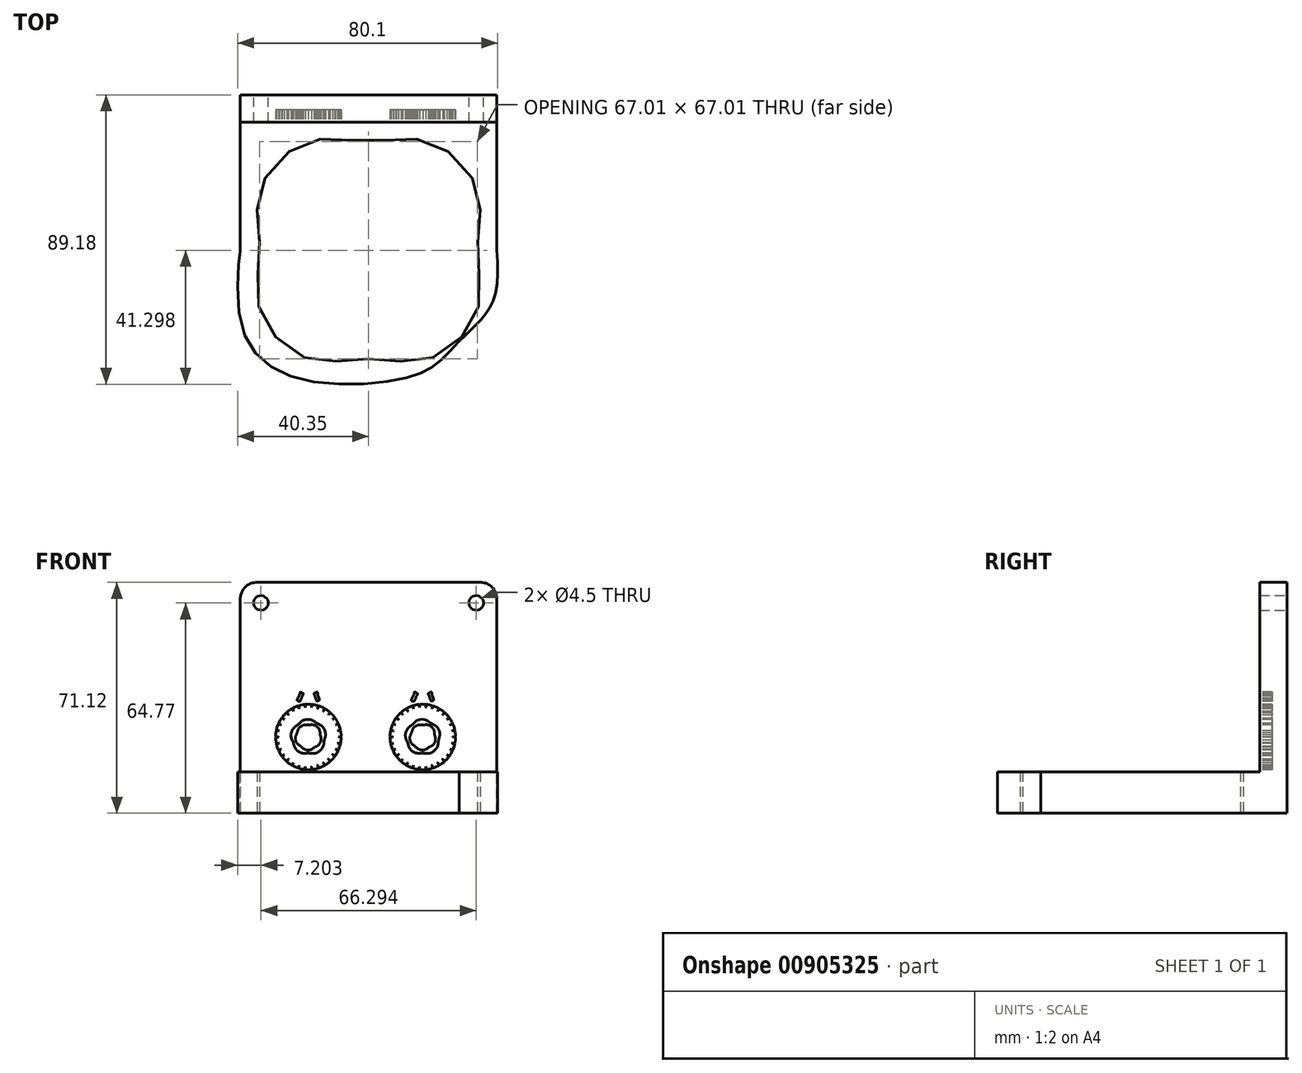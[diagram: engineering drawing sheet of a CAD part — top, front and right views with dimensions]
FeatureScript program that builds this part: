
annotation { "Feature Type Name" : "Feature", "Feature Type Description" : "" }
export const myFeature = defineFeature(function(context is Context, id is Id, definition is map)
    precondition{}
    {
        {
            var Q0;
            Q0=qCreatedBy(makeId("Top.planeOp"),FACE);
            var sketch = newSketch(context, id + "F0", { "sketchPlane" : qUnion([Q0])});
            skFitSpline(sketch, "E0", {"points": [v(-39.5, 39.5) * mm, v(-39.5, 39.5) * mm, v(-39.5, 39.5) * mm, v(-39.5, 38.98) * mm, v(-39.5, 0) * mm, v(-39.5, 0) * mm, v(-39.5, 0) * mm, v(-39.5, -21.82) * mm, v(-21.8, -39.5) * mm, v(10.9, -39.5) * mm, v(20.78, -35.08) * mm, v(27.93, -27.93) * mm]});
            skFitSpline(sketch, "E1", {"points": [v(27.93, -27.93) * mm, v(35.08, -20.78) * mm, v(39.5, -10.91) * mm, v(39.5, 0) * mm, v(39.5, 0) * mm, v(39.5, 0) * mm, v(39.5, 38.98) * mm, v(39.5, 39.5) * mm, v(39.5, 39.5) * mm, v(39.5, 39.5) * mm]});
            skFitSpline(sketch, "E2", {"points": [v(39.5, 39.5) * mm, v(39.5, 39.5) * mm, v(39.5, 39.5) * mm, v(38.99, 39.5) * mm, v(-38.99, 39.5) * mm, v(-39.5, 39.5) * mm, v(-39.5, 39.5) * mm, v(-39.5, 39.5) * mm]});
            skFitSpline(sketch, "E3", {"points": [v(0, -33.5) * mm, v(-18.5, -33.5) * mm, v(-33.5, -18.5) * mm, v(-33.5, 0) * mm, v(-33.5, 18.5) * mm, v(-18.5, 33.5) * mm, v(0, 33.5) * mm, v(18.5, 33.5) * mm, v(33.5, 18.5) * mm, v(33.5, 0) * mm, v(33.5, -18.5) * mm, v(18.5, -33.5) * mm, v(0, -33.5) * mm]});
            skSolve(sketch);
        }
        {
            var Q0;
            Q0=makeQuery(id+"F0.imprint","IMPRINT",FACE,{"disambiguationData":[TD([[makeQuery(id+"F0.imprint","IMPRINT",EDGE,{"derivedFrom":sQuery(id+"F0.wireOp",EDGE,"E0")}),1.0]])]});
            extrude(context, id + "F1", {"entities" : qUnion([Q0]), "depth" : 12.7 * mm, "offsetDistance" : 25.4 * mm});
        }
        {
            var Q0;
            Q0=makeQuery(id+"F1.opExtrude","SWEPT_FACE",FACE,{"disambiguationData":[OSD([sQuery(id+"F0.wireOp",EDGE,"E2")])]});
            var sketch = newSketch(context, id + "F2", { "sketchPlane" : qUnion([Q0])});
            skLineSegment(sketch, "E4.bottom", {"start": v(-39.5, 0) * mm, "end": v(39.5, 0) * mm});
            skLineSegment(sketch, "E4.top", {"start": v(-39.5, 71.12) * mm, "end": v(39.5, 71.12) * mm});
            skLineSegment(sketch, "E4.left", {"start": v(-39.5, 0) * mm, "end": v(-39.5, 71.12) * mm});
            skLineSegment(sketch, "E4.right", {"start": v(39.5, 0) * mm, "end": v(39.5, 71.12) * mm});
            skSolve(sketch);
        }
        {
            var Q0;
            {var subQ0=sQuery(id+"F2.wireOp",EDGE,"E4.top");Q0=makeQuery(id+"F2.imprint","IMPRINT",FACE,{"disambiguationData":[TD([[makeQuery(id+"F2.imprint","IMPRINT",EDGE,{"derivedFrom":subQ0}),-1.0]])]});}
            var Q1;
            {var subQ0=sQuery(id+"F2.wireOp",EDGE,"E4.bottom");Q1=makeQuery(id+"F2.imprint","IMPRINT",FACE,{"disambiguationData":[TD([[makeQuery(id+"F2.imprint","IMPRINT",EDGE,{"derivedFrom":subQ0}),1.0]])]});}
            extrude(context, id + "F3", {"entities" : qUnion([Q0, Q1]), "operationType" : NewBodyOperationType.ADD, "depth" : 8.38 * mm, "offsetDistance" : 25.4 * mm});
        }
        {
            var Q0;
            Q0=makeQuery(id+"F3.opExtrude","CAP_FACE",FACE,{"disambiguationData":[OSD([sQuery(id+"F2.wireOp",EDGE,"E4.bottom"),sQuery(id+"F2.wireOp",EDGE,"E4.top"),sQuery(id+"F2.wireOp",EDGE,"E4.left"),sQuery(id+"F2.wireOp",EDGE,"E4.right")])],"isStart":true});
            var sketch = newSketch(context, id + "F4", { "sketchPlane" : qUnion([Q0])});
            skFitSpline(sketch, "E5", {"points": [v(-16.3, 37.14) * mm, v(-16.53, 37.06) * mm, v(-16.78, 36.97) * mm, v(-16.74, 36.67) * mm]});
            skFitSpline(sketch, "E6", {"points": [v(-16.74, 36.67) * mm, v(-16.73, 36.54) * mm, v(-16.65, 36.4) * mm, v(-16.61, 36.28) * mm]});
            skFitSpline(sketch, "E7", {"points": [v(-16.61, 36.28) * mm, v(-16.45, 35.85) * mm, v(-16.3, 35.4) * mm, v(-16.13, 34.98) * mm]});
            skFitSpline(sketch, "E8", {"points": [v(-16.13, 34.98) * mm, v(-16.07, 34.8) * mm, v(-15.98, 34.64) * mm, v(-15.77, 34.63) * mm]});
            skFitSpline(sketch, "E9", {"points": [v(-15.77, 34.63) * mm, v(-15.54, 34.61) * mm, v(-15.22, 34.78) * mm, v(-15.19, 35.01) * mm]});
            skFitSpline(sketch, "E10", {"points": [v(-15.19, 35.01) * mm, v(-15.17, 35.15) * mm, v(-15.24, 35.3) * mm, v(-15.29, 35.42) * mm]});
            skFitSpline(sketch, "E11", {"points": [v(-15.29, 35.42) * mm, v(-15.37, 35.65) * mm, v(-15.46, 35.88) * mm, v(-15.54, 36.11) * mm]});
            skFitSpline(sketch, "E12", {"points": [v(-15.54, 36.11) * mm, v(-15.65, 36.42) * mm, v(-15.81, 37.32) * mm, v(-16.3, 37.14) * mm]});
            skFitSpline(sketch, "E13", {"points": [v(-20.56, 37.1) * mm, v(-21.01, 37.32) * mm, v(-21.2, 36.62) * mm, v(-21.33, 36.34) * mm]});
            skFitSpline(sketch, "E14", {"points": [v(-21.33, 36.34) * mm, v(-21.5, 35.98) * mm, v(-21.7, 35.63) * mm, v(-21.83, 35.26) * mm]});
            skFitSpline(sketch, "E15", {"points": [v(-21.83, 35.26) * mm, v(-22, 34.76) * mm, v(-21.22, 34.43) * mm, v(-20.96, 34.89) * mm]});
            skFitSpline(sketch, "E16", {"points": [v(-20.96, 34.89) * mm, v(-20.75, 35.26) * mm, v(-20.6, 35.68) * mm, v(-20.41, 36.06) * mm]});
            skFitSpline(sketch, "E17", {"points": [v(-20.41, 36.06) * mm, v(-20.34, 36.21) * mm, v(-20.25, 36.37) * mm, v(-20.2, 36.52) * mm, v(-20.08, 36.85) * mm, v(-20.3, 36.99) * mm, v(-20.56, 37.1) * mm]});
            skFitSpline(sketch, "E18", {"points": [v(-19.4, 35.5) * mm, v(-18.9, 35.5) * mm, v(-18.4, 35.5) * mm, v(-17.91, 35.5) * mm, v(-17.84, 35.5) * mm, v(-17.7, 35.47) * mm, v(-17.63, 35.5) * mm]});
            skFitSpline(sketch, "E19", {"points": [v(-17.63, 35.5) * mm, v(-17.56, 35.53) * mm, v(-17.6, 35.5) * mm, v(-17.56, 35.58) * mm]});
            skFitSpline(sketch, "E20", {"points": [v(-17.56, 35.58) * mm, v(-17.43, 35.76) * mm, v(-17.38, 36.08) * mm, v(-17.3, 36.29) * mm]});
            skFitSpline(sketch, "E21", {"points": [v(-17.3, 36.29) * mm, v(-17.43, 36.29) * mm, v(-17.55, 36.29) * mm, v(-17.68, 36.29) * mm]});
            skFitSpline(sketch, "E22", {"points": [v(-17.68, 36.29) * mm, v(-17.57, 36.66) * mm, v(-17.65, 37.16) * mm, v(-17.65, 37.54) * mm, v(-17.65, 37.95) * mm, v(-17.58, 38.43) * mm, v(-17.67, 38.83) * mm]});
            skFitSpline(sketch, "E23", {"points": [v(-17.67, 38.83) * mm, v(-17.75, 39.18) * mm, v(-18.06, 39.26) * mm, v(-18.38, 39.26) * mm, v(-18.65, 39.26) * mm, v(-18.96, 39.3) * mm, v(-19.16, 39.1) * mm]});
            skFitSpline(sketch, "E24", {"points": [v(-19.16, 39.1) * mm, v(-19.45, 38.8) * mm, v(-19.33, 38.14) * mm, v(-19.33, 37.78) * mm, v(-19.33, 37.47) * mm, v(-19.33, 37.16) * mm, v(-19.33, 36.85) * mm, v(-19.33, 36.68) * mm, v(-19.35, 36.46) * mm, v(-19.3, 36.29) * mm]});
            skFitSpline(sketch, "E25", {"points": [v(-19.3, 36.29) * mm, v(-19.42, 36.29) * mm, v(-19.55, 36.29) * mm, v(-19.67, 36.29) * mm]});
            skFitSpline(sketch, "E26", {"points": [v(-19.67, 36.29) * mm, v(-19.58, 36.03) * mm, v(-19.49, 35.76) * mm, v(-19.4, 35.5) * mm]});
            skFitSpline(sketch, "E27", {"points": [v(18.87, 37.14) * mm, v(18.64, 37.06) * mm, v(18.4, 36.97) * mm, v(18.43, 36.67) * mm]});
            skFitSpline(sketch, "E28", {"points": [v(18.43, 36.67) * mm, v(18.44, 36.54) * mm, v(18.52, 36.4) * mm, v(18.56, 36.28) * mm]});
            skFitSpline(sketch, "E29", {"points": [v(18.56, 36.28) * mm, v(18.72, 35.85) * mm, v(18.87, 35.4) * mm, v(19.04, 34.98) * mm]});
            skFitSpline(sketch, "E30", {"points": [v(19.04, 34.98) * mm, v(19.1, 34.8) * mm, v(19.2, 34.64) * mm, v(19.4, 34.63) * mm]});
            skFitSpline(sketch, "E31", {"points": [v(19.4, 34.63) * mm, v(19.63, 34.61) * mm, v(19.95, 34.78) * mm, v(19.98, 35.01) * mm]});
            skFitSpline(sketch, "E32", {"points": [v(19.98, 35.01) * mm, v(20, 35.15) * mm, v(19.93, 35.3) * mm, v(19.88, 35.42) * mm]});
            skFitSpline(sketch, "E33", {"points": [v(19.88, 35.42) * mm, v(19.8, 35.65) * mm, v(19.72, 35.88) * mm, v(19.63, 36.11) * mm]});
            skFitSpline(sketch, "E34", {"points": [v(19.63, 36.11) * mm, v(19.52, 36.42) * mm, v(19.36, 37.32) * mm, v(18.87, 37.14) * mm]});
            skFitSpline(sketch, "E35", {"points": [v(14.6, 37.1) * mm, v(14.16, 37.32) * mm, v(13.97, 36.62) * mm, v(13.84, 36.34) * mm, v(13.68, 35.98) * mm, v(13.47, 35.63) * mm, v(13.34, 35.26) * mm]});
            skFitSpline(sketch, "E36", {"points": [v(13.34, 35.26) * mm, v(13.16, 34.76) * mm, v(13.95, 34.43) * mm, v(14.21, 34.89) * mm]});
            skFitSpline(sketch, "E37", {"points": [v(14.21, 34.89) * mm, v(14.42, 35.26) * mm, v(14.58, 35.68) * mm, v(14.76, 36.06) * mm, v(14.83, 36.21) * mm, v(14.92, 36.37) * mm, v(14.97, 36.52) * mm, v(15.09, 36.85) * mm, v(14.87, 36.99) * mm, v(14.6, 37.1) * mm]});
            skFitSpline(sketch, "E38", {"points": [v(15.78, 35.5) * mm, v(16.27, 35.5) * mm, v(16.77, 35.5) * mm, v(17.26, 35.5) * mm, v(17.33, 35.5) * mm, v(17.47, 35.47) * mm, v(17.54, 35.5) * mm]});
            skFitSpline(sketch, "E39", {"points": [v(17.54, 35.5) * mm, v(17.61, 35.53) * mm, v(17.56, 35.5) * mm, v(17.62, 35.58) * mm]});
            skFitSpline(sketch, "E40", {"points": [v(17.62, 35.58) * mm, v(17.75, 35.76) * mm, v(17.8, 36.08) * mm, v(17.87, 36.29) * mm]});
            skFitSpline(sketch, "E41", {"points": [v(17.87, 36.29) * mm, v(17.74, 36.29) * mm, v(17.62, 36.29) * mm, v(17.5, 36.29) * mm]});
            skFitSpline(sketch, "E42", {"points": [v(17.5, 36.29) * mm, v(17.6, 36.66) * mm, v(17.52, 37.16) * mm, v(17.52, 37.54) * mm, v(17.52, 37.95) * mm, v(17.6, 38.43) * mm, v(17.5, 38.83) * mm]});
            skFitSpline(sketch, "E43", {"points": [v(17.5, 38.83) * mm, v(17.42, 39.18) * mm, v(17.1, 39.26) * mm, v(16.8, 39.26) * mm, v(16.53, 39.26) * mm, v(16.22, 39.3) * mm, v(16, 39.1) * mm]});
            skFitSpline(sketch, "E44", {"points": [v(16, 39.1) * mm, v(15.73, 38.8) * mm, v(15.85, 38.14) * mm, v(15.85, 37.78) * mm, v(15.85, 37.47) * mm, v(15.85, 37.16) * mm, v(15.85, 36.85) * mm, v(15.85, 36.68) * mm, v(15.82, 36.46) * mm, v(15.87, 36.29) * mm]});
            skFitSpline(sketch, "E45", {"points": [v(15.87, 36.29) * mm, v(15.75, 36.29) * mm, v(15.62, 36.29) * mm, v(15.5, 36.29) * mm]});
            skFitSpline(sketch, "E46", {"points": [v(15.5, 36.29) * mm, v(15.6, 36.03) * mm, v(15.68, 35.76) * mm, v(15.78, 35.5) * mm]});
            skFitSpline(sketch, "E47", {"points": [v(-25.13, 35.02) * mm, v(-24.72, 36.98) * mm, v(-23.7, 39.03) * mm, v(-22.15, 40.32) * mm]});
            skFitSpline(sketch, "E48", {"points": [v(-22.15, 40.32) * mm, v(-20.8, 41.44) * mm, v(-19.07, 41.82) * mm, v(-17.35, 41.52) * mm]});
            skFitSpline(sketch, "E49", {"points": [v(-17.35, 41.52) * mm, v(-15.7, 41.24) * mm, v(-14.3, 40.3) * mm, v(-13.36, 38.94) * mm]});
            skFitSpline(sketch, "E50", {"points": [v(-13.36, 38.94) * mm, v(-12.68, 37.95) * mm, v(-12.2, 36.77) * mm, v(-12.02, 35.57) * mm]});
            skFitSpline(sketch, "E51", {"points": [v(-12.02, 35.57) * mm, v(-12, 35.46) * mm, v(-12.03, 35.14) * mm, v(-11.97, 35.05) * mm]});
            skFitSpline(sketch, "E52", {"points": [v(-11.97, 35.05) * mm, v(-11.91, 34.96) * mm, v(-11.5, 35.02) * mm, v(-11.38, 35.02) * mm, v(-11.04, 35.02) * mm, v(-10.7, 35.02) * mm, v(-10.35, 35.02) * mm, v(-10.3, 35.02) * mm, v(-10.13, 34.99) * mm, v(-10.1, 35.02) * mm]});
            skFitSpline(sketch, "E53", {"points": [v(-10.1, 35.02) * mm, v(-10.05, 35.05) * mm, v(-10.08, 35.27) * mm, v(-10.08, 35.34) * mm, v(-10.08, 35.67) * mm, v(-10.14, 35.66) * mm, v(-9.86, 35.66) * mm, v(-9.58, 35.66) * mm, v(-9.3, 35.66) * mm, v(-9.01, 35.66) * mm, v(-7.96, 35.66) * mm, v(-6.9, 35.66) * mm, v(-5.85, 35.66) * mm, v(-2.95, 35.66) * mm, v(-0.06, 35.66) * mm, v(2.84, 35.66) * mm, v(4.06, 35.66) * mm, v(5.28, 35.66) * mm, v(6.5, 35.66) * mm, v(6.91, 35.66) * mm, v(7.32, 35.66) * mm, v(7.72, 35.66) * mm, v(7.91, 35.66) * mm, v(8.21, 35.72) * mm, v(8.4, 35.66) * mm]});
            skFitSpline(sketch, "E54", {"points": [v(8.4, 35.66) * mm, v(8.42, 35.65) * mm, v(8.46, 35.67) * mm, v(8.48, 35.65) * mm]});
            skFitSpline(sketch, "E55", {"points": [v(8.48, 35.65) * mm, v(8.6, 35.55) * mm, v(8.37, 35.1) * mm, v(8.5, 35.02) * mm]});
            skFitSpline(sketch, "E56", {"points": [v(8.5, 35.02) * mm, v(8.56, 34.98) * mm, v(8.76, 35.02) * mm, v(8.82, 35.02) * mm, v(9, 35.02) * mm, v(9.2, 35.02) * mm, v(9.38, 35.02) * mm, v(9.55, 35.02) * mm, v(9.72, 35.02) * mm, v(9.89, 35.02) * mm, v(9.95, 35.02) * mm, v(10.16, 34.98) * mm, v(10.21, 35.02) * mm]});
            skFitSpline(sketch, "E57", {"points": [v(10.21, 35.02) * mm, v(10.28, 35.07) * mm, v(10.27, 35.35) * mm, v(10.28, 35.45) * mm]});
            skFitSpline(sketch, "E58", {"points": [v(10.28, 35.45) * mm, v(10.34, 35.85) * mm, v(10.43, 36.24) * mm, v(10.54, 36.63) * mm]});
            skFitSpline(sketch, "E59", {"points": [v(10.54, 36.63) * mm, v(10.87, 37.8) * mm, v(11.43, 38.94) * mm, v(12.29, 39.83) * mm]});
            skFitSpline(sketch, "E60", {"points": [v(12.29, 39.83) * mm, v(13.43, 41.03) * mm, v(15.01, 41.59) * mm, v(16.65, 41.62) * mm]});
            skFitSpline(sketch, "E61", {"points": [v(16.65, 41.62) * mm, v(18.33, 41.65) * mm, v(19.99, 41.16) * mm, v(21.2, 39.97) * mm]});
            skFitSpline(sketch, "E62", {"points": [v(21.2, 39.97) * mm, v(22.1, 39.1) * mm, v(22.7, 37.96) * mm, v(23.05, 36.77) * mm]});
            skFitSpline(sketch, "E63", {"points": [v(23.05, 36.77) * mm, v(23.17, 36.36) * mm, v(23.26, 35.95) * mm, v(23.33, 35.53) * mm, v(23.34, 35.45) * mm, v(23.33, 35.07) * mm, v(23.4, 35.02) * mm]});
            skFitSpline(sketch, "E64", {"points": [v(23.4, 35.02) * mm, v(23.47, 34.95) * mm, v(23.94, 35.02) * mm, v(24.04, 35.02) * mm, v(24.34, 35.02) * mm, v(24.73, 34.95) * mm, v(25.02, 35.02) * mm]});
            skFitSpline(sketch, "E65", {"points": [v(25.02, 35.02) * mm, v(25.14, 35.05) * mm, v(25.12, 35.05) * mm, v(25.21, 35.17) * mm]});
            skFitSpline(sketch, "E66", {"points": [v(25.21, 35.17) * mm, v(25.37, 35.38) * mm, v(25.55, 35.58) * mm, v(25.75, 35.76) * mm]});
            skFitSpline(sketch, "E67", {"points": [v(25.75, 35.76) * mm, v(26.44, 36.37) * mm, v(27.31, 36.73) * mm, v(28.24, 36.73) * mm]});
            skFitSpline(sketch, "E68", {"points": [v(28.24, 36.73) * mm, v(27.97, 37.36) * mm, v(27.93, 38.12) * mm, v(27.89, 38.78) * mm]});
            skFitSpline(sketch, "E69", {"points": [v(27.89, 38.78) * mm, v(27.83, 39.68) * mm, v(27.89, 40.58) * mm, v(27.72, 41.47) * mm]});
            skFitSpline(sketch, "E70", {"points": [v(27.72, 41.47) * mm, v(27.58, 42.23) * mm, v(27.33, 43) * mm, v(26.92, 43.66) * mm, v(26.64, 44.1) * mm, v(26.24, 44.59) * mm, v(25.71, 44.74) * mm, v(25.39, 44.84) * mm, v(25, 44.79) * mm, v(24.66, 44.79) * mm, v(23.12, 44.79) * mm, v(21.59, 44.79) * mm, v(20.05, 44.79) * mm, v(19.8, 44.79) * mm, v(19.55, 44.79) * mm, v(19.3, 44.79) * mm, v(19.13, 44.79) * mm, v(18.86, 44.74) * mm, v(18.7, 44.8) * mm]});
            skFitSpline(sketch, "E71", {"points": [v(18.7, 44.8) * mm, v(18.67, 44.8) * mm, v(18.65, 44.83) * mm, v(18.62, 44.84) * mm]});
            skFitSpline(sketch, "E72", {"points": [v(18.62, 44.84) * mm, v(18.46, 44.93) * mm, v(18.3, 45.06) * mm, v(18.15, 45.17) * mm]});
            skFitSpline(sketch, "E73", {"points": [v(18.15, 45.17) * mm, v(17.5, 45.61) * mm, v(16.86, 46.05) * mm, v(16.22, 46.5) * mm, v(14.62, 47.6) * mm, v(13.03, 48.69) * mm, v(11.44, 49.78) * mm]});
            skFitSpline(sketch, "E74", {"points": [v(11.44, 49.78) * mm, v(11.17, 49.96) * mm, v(10.9, 50.15) * mm, v(10.63, 50.33) * mm]});
            skFitSpline(sketch, "E75", {"points": [v(10.63, 50.33) * mm, v(10.5, 50.42) * mm, v(10.32, 50.5) * mm, v(10.2, 50.63) * mm]});
            skFitSpline(sketch, "E76", {"points": [v(10.2, 50.63) * mm, v(10.1, 50.73) * mm, v(10.14, 50.81) * mm, v(10.14, 50.97) * mm, v(10.14, 51.45) * mm, v(10.14, 51.93) * mm, v(10.14, 52.41) * mm, v(10.14, 52.67) * mm, v(10.24, 53.2) * mm, v(10, 53.38) * mm]});
            skFitSpline(sketch, "E77", {"points": [v(10, 53.38) * mm, v(9.87, 53.5) * mm, v(9.5, 53.5) * mm, v(9.33, 53.43) * mm]});
            skFitSpline(sketch, "E78", {"points": [v(9.33, 53.43) * mm, v(9.19, 53.36) * mm, v(9.15, 53.22) * mm, v(9.14, 53.07) * mm]});
            skFitSpline(sketch, "E79", {"points": [v(9.14, 53.07) * mm, v(9.1, 52.54) * mm, v(9.14, 51.98) * mm, v(9.14, 51.44) * mm, v(9.14, 49.55) * mm, v(9.14, 47.65) * mm, v(9.14, 45.76) * mm, v(9.14, 45.5) * mm, v(9.14, 45.24) * mm, v(9.14, 44.98) * mm, v(9.14, 44.95) * mm, v(9.16, 44.83) * mm, v(9.14, 44.8) * mm]});
            skFitSpline(sketch, "E80", {"points": [v(9.14, 44.8) * mm, v(9.08, 44.73) * mm, v(8.57, 44.8) * mm, v(8.44, 44.8) * mm, v(8.19, 44.8) * mm, v(8.05, 44.7) * mm, v(8.05, 44.94) * mm, v(8.05, 45.2) * mm, v(8.05, 45.47) * mm, v(8.05, 45.74) * mm, v(8.05, 47.58) * mm, v(8.05, 49.42) * mm, v(8.05, 51.27) * mm, v(8.05, 51.43) * mm, v(8.12, 51.78) * mm, v(8.05, 51.94) * mm]});
            skFitSpline(sketch, "E81", {"points": [v(8.05, 51.94) * mm, v(7.99, 52.07) * mm, v(7.62, 52) * mm, v(7.46, 52) * mm, v(7.27, 52) * mm, v(6.66, 51.9) * mm, v(6.57, 52.06) * mm]});
            skFitSpline(sketch, "E82", {"points": [v(6.57, 52.06) * mm, v(6.5, 52.2) * mm, v(6.5, 52.47) * mm, v(6.47, 52.62) * mm]});
            skFitSpline(sketch, "E83", {"points": [v(6.47, 52.62) * mm, v(6.43, 52.86) * mm, v(6.4, 53.1) * mm, v(6.35, 53.34) * mm]});
            skFitSpline(sketch, "E84", {"points": [v(6.35, 53.34) * mm, v(6.28, 53.71) * mm, v(6.28, 54.14) * mm, v(5.8, 54.12) * mm]});
            skFitSpline(sketch, "E85", {"points": [v(5.8, 54.12) * mm, v(5.8, 56.67) * mm, v(6.23, 59.23) * mm, v(7.36, 61.53) * mm]});
            skFitSpline(sketch, "E86", {"points": [v(7.36, 61.53) * mm, v(8.43, 63.72) * mm, v(10.08, 65.55) * mm, v(12.05, 66.98) * mm]});
            skFitSpline(sketch, "E87", {"points": [v(12.05, 66.98) * mm, v(12.6, 67.38) * mm, v(13.16, 67.75) * mm, v(13.75, 68.09) * mm, v(14.03, 68.25) * mm, v(14.31, 68.4) * mm, v(14.6, 68.55) * mm, v(14.86, 68.7) * mm, v(15.44, 68.84) * mm, v(15.35, 69.23) * mm]});
            skFitSpline(sketch, "E88", {"points": [v(15.35, 69.23) * mm, v(15.2, 69.9) * mm, v(13.99, 69.03) * mm, v(13.67, 68.85) * mm]});
            skFitSpline(sketch, "E89", {"points": [v(13.67, 68.85) * mm, v(13.07, 68.52) * mm, v(12.5, 68.15) * mm, v(11.93, 67.76) * mm]});
            skFitSpline(sketch, "E90", {"points": [v(11.93, 67.76) * mm, v(9.93, 66.37) * mm, v(8.2, 64.6) * mm, v(7.03, 62.45) * mm]});
            skFitSpline(sketch, "E91", {"points": [v(7.03, 62.45) * mm, v(5.82, 60.24) * mm, v(5.24, 57.75) * mm, v(5.12, 55.25) * mm]});
            skFitSpline(sketch, "E92", {"points": [v(5.12, 55.25) * mm, v(5.1, 54.94) * mm, v(5.1, 54.62) * mm, v(5.09, 54.3) * mm]});
            skFitSpline(sketch, "E93", {"points": [v(5.09, 54.3) * mm, v(5.09, 54.09) * mm, v(5.1, 54.17) * mm, v(4.96, 54.12) * mm]});
            skFitSpline(sketch, "E94", {"points": [v(4.96, 54.12) * mm, v(4.79, 54.07) * mm, v(4.67, 54.05) * mm, v(4.61, 53.85) * mm]});
            skFitSpline(sketch, "E95", {"points": [v(4.61, 53.85) * mm, v(4.52, 53.54) * mm, v(4.5, 53.17) * mm, v(4.44, 52.85) * mm]});
            skFitSpline(sketch, "E96", {"points": [v(4.44, 52.85) * mm, v(4.41, 52.66) * mm, v(4.38, 52.46) * mm, v(4.34, 52.26) * mm, v(4.33, 52.22) * mm, v(4.33, 52.03) * mm, v(4.3, 52) * mm]});
            skFitSpline(sketch, "E97", {"points": [v(4.3, 52) * mm, v(4.26, 51.97) * mm, v(4.07, 52) * mm, v(4.03, 52) * mm, v(0.92, 52) * mm, v(-2.19, 52) * mm, v(-5.3, 52) * mm, v(-5.58, 52) * mm, v(-5.95, 52.06) * mm, v(-6.23, 52) * mm]});
            skFitSpline(sketch, "E98", {"points": [v(-6.23, 52) * mm, v(-6.34, 51.97) * mm, v(-6.46, 51.87) * mm, v(-6.56, 51.82) * mm]});
            skFitSpline(sketch, "E99", {"points": [v(-6.56, 51.82) * mm, v(-6.86, 51.66) * mm, v(-7.15, 51.49) * mm, v(-7.44, 51.32) * mm]});
            skFitSpline(sketch, "E100", {"points": [v(-7.44, 51.32) * mm, v(-9.53, 50.1) * mm, v(-11.62, 48.7) * mm, v(-13.26, 46.91) * mm]});
            skFitSpline(sketch, "E101", {"points": [v(-13.26, 46.91) * mm, v(-13.44, 46.72) * mm, v(-13.6, 46.43) * mm, v(-13.81, 46.26) * mm]});
            skFitSpline(sketch, "E102", {"points": [v(-13.81, 46.26) * mm, v(-13.97, 46.14) * mm, v(-14.3, 46.21) * mm, v(-14.5, 46.2) * mm]});
            skFitSpline(sketch, "E103", {"points": [v(-14.5, 46.2) * mm, v(-14.5, 46.47) * mm, v(-14.43, 46.87) * mm, v(-14.55, 47.1) * mm]});
            skFitSpline(sketch, "E104", {"points": [v(-14.55, 47.1) * mm, v(-14.65, 47.32) * mm, v(-14.87, 47.3) * mm, v(-15.07, 47.3) * mm, v(-15.7, 47.3) * mm, v(-16.33, 47.3) * mm, v(-16.96, 47.3) * mm, v(-17.75, 47.3) * mm, v(-18.54, 47.3) * mm, v(-19.32, 47.3) * mm, v(-19.6, 47.3) * mm, v(-19.9, 47.3) * mm, v(-20.18, 47.3) * mm, v(-20.3, 47.3) * mm, v(-20.45, 47.33) * mm, v(-20.57, 47.3) * mm, v(-21.04, 47.17) * mm, v(-20.74, 46.65) * mm, v(-20.64, 46.37) * mm]});
            skFitSpline(sketch, "E105", {"points": [v(-20.64, 46.37) * mm, v(-20.53, 46.05) * mm, v(-20.42, 45.72) * mm, v(-20.3, 45.4) * mm]});
            skFitSpline(sketch, "E106", {"points": [v(-20.3, 45.4) * mm, v(-22.39, 44.81) * mm, v(-24.63, 43.8) * mm, v(-25.9, 41.97) * mm]});
            skFitSpline(sketch, "E107", {"points": [v(-25.9, 41.97) * mm, v(-27.05, 40.33) * mm, v(-27.54, 38.21) * mm, v(-27, 36.26) * mm]});
            skFitSpline(sketch, "E108", {"points": [v(-27, 36.26) * mm, v(-26.9, 35.9) * mm, v(-26.77, 35.41) * mm, v(-26.55, 35.11) * mm]});
            skFitSpline(sketch, "E109", {"points": [v(-26.55, 35.11) * mm, v(-26.45, 34.98) * mm, v(-26.37, 35.02) * mm, v(-26.18, 35.02) * mm, v(-25.83, 35.02) * mm, v(-25.48, 35.02) * mm, v(-25.13, 35.02) * mm]});
            skFitSpline(sketch, "E110", {"points": [v(10.14, 49.46) * mm, v(12.12, 48.1) * mm, v(14.1, 46.73) * mm, v(16.1, 45.37) * mm]});
            skFitSpline(sketch, "E111", {"points": [v(16.1, 45.37) * mm, v(16.37, 45.17) * mm, v(16.65, 44.98) * mm, v(16.93, 44.79) * mm]});
            skFitSpline(sketch, "E112", {"points": [v(16.93, 44.79) * mm, v(15.57, 44.79) * mm, v(14.21, 44.79) * mm, v(12.85, 44.79) * mm, v(12.26, 44.79) * mm, v(11.68, 44.79) * mm, v(11.1, 44.79) * mm, v(11, 44.79) * mm, v(10.78, 44.77) * mm, v(10.57, 44.76) * mm]});
            skFitSpline(sketch, "E113", {"points": [v(10.57, 44.76) * mm, v(10.37, 44.76) * mm, v(10.17, 44.77) * mm, v(10.14, 44.83) * mm, v(10.09, 44.93) * mm, v(10.14, 45.2) * mm, v(10.14, 45.3) * mm, v(10.14, 45.59) * mm, v(10.14, 45.87) * mm, v(10.14, 46.16) * mm, v(10.14, 46.84) * mm, v(10.14, 47.52) * mm, v(10.14, 48.2) * mm, v(10.14, 48.61) * mm, v(10.14, 49.04) * mm, v(10.14, 49.46) * mm]});
            skFitSpline(sketch, "E114", {"points": [v(-5.58, 50.61) * mm, v(-3.95, 50.61) * mm, v(-2.31, 50.61) * mm, v(-0.68, 50.61) * mm, v(-0.35, 50.61) * mm, v(-0.01, 50.61) * mm, v(0.32, 50.61) * mm, v(0.5, 50.61) * mm, v(0.5, 50.65) * mm, v(0.5, 50.48) * mm, v(0.55, 49.58) * mm, v(0.5, 48.67) * mm, v(0.5, 47.77) * mm, v(0.5, 47.34) * mm, v(0.5, 46.92) * mm, v(0.5, 46.5) * mm, v(0.5, 46.4) * mm, v(0.54, 46.26) * mm, v(0.47, 46.22) * mm]});
            skFitSpline(sketch, "E115", {"points": [v(0.47, 46.22) * mm, v(0.37, 46.17) * mm, v(0.09, 46.22) * mm, v(-0.02, 46.22) * mm, v(-0.17, 46.22) * mm, v(-0.32, 46.22) * mm, v(-0.48, 46.22) * mm]});
            skFitSpline(sketch, "E116", {"points": [v(-0.48, 46.22) * mm, v(-0.63, 46.22) * mm, v(-0.79, 46.22) * mm, v(-0.94, 46.22) * mm, v(-2.94, 46.22) * mm, v(-4.95, 46.22) * mm, v(-6.95, 46.22) * mm, v(-7.9, 46.22) * mm, v(-8.83, 46.22) * mm, v(-9.78, 46.22) * mm, v(-10.1, 46.22) * mm, v(-10.42, 46.22) * mm, v(-10.75, 46.22) * mm, v(-10.9, 46.22) * mm, v(-11.15, 46.17) * mm, v(-11.3, 46.22) * mm]});
            skFitSpline(sketch, "E117", {"points": [v(-11.3, 46.22) * mm, v(-11.31, 46.23) * mm, v(-11.35, 46.22) * mm, v(-11.37, 46.22) * mm]});
            skFitSpline(sketch, "E118", {"points": [v(-11.37, 46.22) * mm, v(-10.42, 47.46) * mm, v(-9.1, 48.43) * mm, v(-7.82, 49.28) * mm, v(-7.1, 49.76) * mm, v(-6.35, 50.21) * mm, v(-5.58, 50.61) * mm]});
            skFitSpline(sketch, "E119", {"points": [v(-18.52, 18.54) * mm, v(-20.58, 18.54) * mm, v(-22.46, 19.85) * mm, v(-23.17, 21.78) * mm]});
            skFitSpline(sketch, "E120", {"points": [v(-23.17, 21.78) * mm, v(-23.88, 23.73) * mm, v(-23.27, 25.97) * mm, v(-21.67, 27.3) * mm]});
            skFitSpline(sketch, "E121", {"points": [v(-21.67, 27.3) * mm, v(-20.07, 28.61) * mm, v(-17.74, 28.78) * mm, v(-15.96, 27.7) * mm]});
            skFitSpline(sketch, "E122", {"points": [v(-15.96, 27.7) * mm, v(-14.2, 26.63) * mm, v(-13.27, 24.51) * mm, v(-13.68, 22.48) * mm]});
            skFitSpline(sketch, "E123", {"points": [v(-13.68, 22.48) * mm, v(-14.15, 20.21) * mm, v(-16.2, 18.54) * mm, v(-18.52, 18.54) * mm]});
            skFitSpline(sketch, "E124", {"points": [v(-18.52, 27.16) * mm, v(-20.05, 27.16) * mm, v(-21.45, 26.19) * mm, v(-21.98, 24.76) * mm]});
            skFitSpline(sketch, "E125", {"points": [v(-21.98, 24.76) * mm, v(-22.53, 23.3) * mm, v(-22.07, 21.61) * mm, v(-20.87, 20.62) * mm]});
            skFitSpline(sketch, "E126", {"points": [v(-20.87, 20.62) * mm, v(-19.68, 19.64) * mm, v(-17.95, 19.51) * mm, v(-16.63, 20.3) * mm]});
            skFitSpline(sketch, "E127", {"points": [v(-16.63, 20.3) * mm, v(-15.31, 21.1) * mm, v(-14.6, 22.67) * mm, v(-14.9, 24.18) * mm]});
            skFitSpline(sketch, "E128", {"points": [v(-14.9, 24.18) * mm, v(-15.23, 25.89) * mm, v(-16.78, 27.16) * mm, v(-18.52, 27.16) * mm]});
            skFitSpline(sketch, "E129", {"points": [v(-8.75, 23.41) * mm, v(-8.75, 23.41) * mm, v(-8.75, 23.41) * mm, v(-8.8, 23.42) * mm, v(-9.3, 23.47) * mm, v(-9.36, 23.48) * mm, v(-9.36, 23.48) * mm, v(-9.36, 23.48) * mm]});
            skFitSpline(sketch, "E130", {"points": [v(-9.36, 23.48) * mm, v(-9.36, 23.48) * mm, v(-9.36, 23.48) * mm, v(-9.3, 23.48) * mm, v(-8.75, 23.54) * mm, v(-8.75, 23.54) * mm, v(-8.74, 23.54) * mm, v(-8.55, 23.56) * mm, v(-8.41, 23.73) * mm, v(-8.43, 23.93) * mm, v(-8.43, 23.93) * mm, v(-8.43, 23.94) * mm, v(-8.56, 25.12) * mm, v(-8.56, 25.13) * mm, v(-8.56, 25.13) * mm, v(-8.58, 25.32) * mm, v(-8.75, 25.46) * mm, v(-8.94, 25.44) * mm, v(-8.95, 25.44) * mm, v(-8.95, 25.44) * mm, v(-9.5, 25.39) * mm, v(-9.56, 25.38) * mm, v(-9.56, 25.38) * mm, v(-9.56, 25.38) * mm]});
            skFitSpline(sketch, "E131", {"points": [v(-9.56, 25.38) * mm, v(-9.56, 25.38) * mm, v(-9.56, 25.38) * mm, v(-9.5, 25.4) * mm, v(-8.98, 25.57) * mm, v(-8.97, 25.57) * mm, v(-8.97, 25.57) * mm, v(-8.79, 25.63) * mm, v(-8.69, 25.83) * mm, v(-8.75, 26.01) * mm, v(-8.75, 26.02) * mm, v(-8.75, 26.03) * mm, v(-9.12, 27.16) * mm, v(-9.12, 27.17) * mm, v(-9.12, 27.17) * mm, v(-9.18, 27.35) * mm, v(-9.38, 27.45) * mm, v(-9.56, 27.4) * mm, v(-9.56, 27.4) * mm, v(-9.57, 27.4) * mm, v(-10.1, 27.22) * mm, v(-10.15, 27.2) * mm, v(-10.15, 27.2) * mm, v(-10.15, 27.2) * mm]});
            skFitSpline(sketch, "E132", {"points": [v(-10.15, 27.2) * mm, v(-10.15, 27.2) * mm, v(-10.15, 27.2) * mm, v(-10.1, 27.23) * mm, v(-9.62, 27.5) * mm, v(-9.62, 27.51) * mm, v(-9.62, 27.51) * mm, v(-9.45, 27.61) * mm, v(-9.4, 27.82) * mm, v(-9.49, 28) * mm, v(-9.49, 28) * mm, v(-9.5, 28) * mm, v(-10.09, 29.03) * mm, v(-10.1, 29.04) * mm, v(-10.1, 29.04) * mm, v(-10.2, 29.2) * mm, v(-10.4, 29.27) * mm, v(-10.57, 29.17) * mm, v(-10.57, 29.17) * mm, v(-10.58, 29.17) * mm, v(-11.06, 28.9) * mm, v(-11.1, 28.86) * mm, v(-11.11, 28.86) * mm, v(-11.11, 28.86) * mm]});
            skFitSpline(sketch, "E133", {"points": [v(-11.11, 28.86) * mm, v(-11.11, 28.86) * mm, v(-11.11, 28.86) * mm, v(-11.06, 28.9) * mm, v(-10.66, 29.27) * mm, v(-10.65, 29.27) * mm, v(-10.65, 29.28) * mm, v(-10.5, 29.4) * mm, v(-10.5, 29.63) * mm, v(-10.62, 29.77) * mm, v(-10.62, 29.77) * mm, v(-10.63, 29.78) * mm, v(-11.43, 30.66) * mm, v(-11.44, 30.67) * mm, v(-11.44, 30.67) * mm, v(-11.57, 30.82) * mm, v(-11.79, 30.83) * mm, v(-11.93, 30.7) * mm, v(-11.93, 30.7) * mm, v(-11.94, 30.7) * mm, v(-12.35, 30.33) * mm, v(-12.4, 30.28) * mm, v(-12.4, 30.28) * mm, v(-12.4, 30.28) * mm]});
            skFitSpline(sketch, "E134", {"points": [v(-12.4, 30.28) * mm, v(-12.4, 30.28) * mm, v(-12.4, 30.28) * mm, v(-12.36, 30.33) * mm, v(-12.03, 30.78) * mm, v(-12.03, 30.78) * mm, v(-12.03, 30.79) * mm, v(-11.92, 30.94) * mm, v(-11.95, 31.16) * mm, v(-12.1, 31.28) * mm, v(-12.1, 31.28) * mm, v(-12.12, 31.28) * mm, v(-13.08, 31.98) * mm, v(-13.09, 31.99) * mm, v(-13.09, 31.99) * mm, v(-13.24, 32.1) * mm, v(-13.46, 32.07) * mm, v(-13.58, 31.91) * mm, v(-13.58, 31.91) * mm, v(-13.58, 31.9) * mm, v(-13.9, 31.46) * mm, v(-13.94, 31.41) * mm, v(-13.94, 31.41) * mm, v(-13.94, 31.4) * mm]});
            skFitSpline(sketch, "E135", {"points": [v(-13.94, 31.4) * mm, v(-13.94, 31.41) * mm, v(-13.94, 31.41) * mm, v(-13.92, 31.47) * mm, v(-13.7, 31.97) * mm, v(-13.7, 31.98) * mm, v(-13.69, 31.98) * mm, v(-13.61, 32.15) * mm, v(-13.7, 32.36) * mm, v(-13.87, 32.44) * mm, v(-13.87, 32.44) * mm, v(-13.88, 32.45) * mm, v(-14.96, 32.93) * mm, v(-14.98, 32.93) * mm, v(-14.98, 32.93) * mm, v(-15.15, 33.01) * mm, v(-15.36, 32.93) * mm, v(-15.44, 32.76) * mm, v(-15.44, 32.75) * mm, v(-15.44, 32.75) * mm, v(-15.67, 32.25) * mm, v(-15.7, 32.2) * mm, v(-15.7, 32.19) * mm, v(-15.7, 32.19) * mm]});
            skFitSpline(sketch, "E136", {"points": [v(-15.7, 32.19) * mm, v(-15.7, 32.2) * mm, v(-15.7, 32.2) * mm, v(-15.68, 32.25) * mm, v(-15.56, 32.79) * mm, v(-15.56, 32.8) * mm, v(-15.56, 32.8) * mm, v(-15.52, 32.99) * mm, v(-15.64, 33.17) * mm, v(-15.83, 33.21) * mm, v(-15.83, 33.21) * mm, v(-15.85, 33.21) * mm, v(-17, 33.46) * mm, v(-17.02, 33.46) * mm, v(-17.02, 33.46) * mm, v(-17.2, 33.5) * mm, v(-17.4, 33.38) * mm, v(-17.44, 33.2) * mm, v(-17.44, 33.2) * mm, v(-17.44, 33.19) * mm, v(-17.55, 32.65) * mm, v(-17.57, 32.59) * mm, v(-17.57, 32.59) * mm, v(-17.57, 32.59) * mm]});
            skFitSpline(sketch, "E137", {"points": [v(-17.57, 32.59) * mm, v(-17.57, 32.59) * mm, v(-17.57, 32.59) * mm, v(-17.57, 32.65) * mm, v(-17.57, 33.2) * mm, v(-17.57, 33.2) * mm, v(-17.57, 33.2) * mm, v(-17.57, 33.4) * mm, v(-17.72, 33.56) * mm, v(-17.92, 33.56) * mm, v(-17.92, 33.56) * mm, v(-17.93, 33.56) * mm, v(-19.12, 33.56) * mm, v(-19.13, 33.56) * mm, v(-19.13, 33.56) * mm, v(-19.32, 33.56) * mm, v(-19.48, 33.4) * mm, v(-19.48, 33.2) * mm, v(-19.48, 33.2) * mm, v(-19.48, 33.2) * mm, v(-19.48, 32.65) * mm, v(-19.48, 32.59) * mm, v(-19.48, 32.59) * mm, v(-19.48, 32.59) * mm]});
            skFitSpline(sketch, "E138", {"points": [v(-19.48, 32.59) * mm, v(-19.48, 32.59) * mm, v(-19.48, 32.59) * mm, v(-19.5, 32.65) * mm, v(-19.6, 33.19) * mm, v(-19.6, 33.2) * mm, v(-19.61, 33.2) * mm, v(-19.65, 33.38) * mm, v(-19.84, 33.5) * mm, v(-20.03, 33.46) * mm, v(-20.03, 33.46) * mm, v(-20.04, 33.46) * mm, v(-21.2, 33.21) * mm, v(-21.21, 33.21) * mm, v(-21.21, 33.21) * mm, v(-21.4, 33.17) * mm, v(-21.52, 32.99) * mm, v(-21.48, 32.8) * mm, v(-21.48, 32.8) * mm, v(-21.48, 32.79) * mm, v(-21.37, 32.25) * mm, v(-21.35, 32.2) * mm, v(-21.35, 32.19) * mm, v(-21.35, 32.19) * mm]});
            skFitSpline(sketch, "E139", {"points": [v(-21.35, 32.19) * mm, v(-21.36, 32.19) * mm, v(-21.36, 32.19) * mm, v(-21.38, 32.25) * mm, v(-21.6, 32.75) * mm, v(-21.6, 32.75) * mm, v(-21.6, 32.76) * mm, v(-21.69, 32.93) * mm, v(-21.9, 33.01) * mm, v(-22.07, 32.93) * mm, v(-22.07, 32.93) * mm, v(-22.08, 32.93) * mm, v(-23.17, 32.45) * mm, v(-23.18, 32.44) * mm, v(-23.18, 32.44) * mm, v(-23.35, 32.36) * mm, v(-23.43, 32.15) * mm, v(-23.36, 31.98) * mm, v(-23.36, 31.98) * mm, v(-23.35, 31.97) * mm, v(-23.13, 31.47) * mm, v(-23.1, 31.41) * mm, v(-23.1, 31.41) * mm, v(-23.1, 31.4) * mm]});
            skFitSpline(sketch, "E140", {"points": [v(-23.1, 31.4) * mm, v(-23.1, 31.41) * mm, v(-23.1, 31.41) * mm, v(-23.14, 31.46) * mm, v(-23.46, 31.9) * mm, v(-23.47, 31.91) * mm, v(-23.47, 31.91) * mm, v(-23.58, 32.07) * mm, v(-23.8, 32.1) * mm, v(-23.96, 31.99) * mm, v(-23.96, 31.99) * mm, v(-23.97, 31.98) * mm, v(-24.93, 31.28) * mm, v(-24.94, 31.28) * mm, v(-24.94, 31.28) * mm, v(-25.1, 31.16) * mm, v(-25.13, 30.94) * mm, v(-25.02, 30.79) * mm, v(-25.02, 30.78) * mm, v(-25.01, 30.78) * mm, v(-24.7, 30.33) * mm, v(-24.65, 30.28) * mm, v(-24.65, 30.28) * mm, v(-24.65, 30.28) * mm]});
            skFitSpline(sketch, "E141", {"points": [v(-24.65, 30.28) * mm, v(-24.65, 30.28) * mm, v(-24.65, 30.28) * mm, v(-24.7, 30.33) * mm, v(-25.1, 30.7) * mm, v(-25.11, 30.7) * mm, v(-25.12, 30.7) * mm, v(-25.26, 30.83) * mm, v(-25.48, 30.82) * mm, v(-25.61, 30.67) * mm, v(-25.61, 30.67) * mm, v(-25.62, 30.66) * mm, v(-26.41, 29.78) * mm, v(-26.42, 29.77) * mm, v(-26.42, 29.77) * mm, v(-26.55, 29.63) * mm, v(-26.54, 29.4) * mm, v(-26.4, 29.28) * mm, v(-26.4, 29.27) * mm, v(-26.4, 29.27) * mm, v(-25.98, 28.9) * mm, v(-25.94, 28.86) * mm, v(-25.94, 28.86) * mm, v(-25.94, 28.86) * mm]});
            skFitSpline(sketch, "E142", {"points": [v(-25.94, 28.86) * mm, v(-25.94, 28.86) * mm, v(-25.94, 28.86) * mm, v(-25.99, 28.9) * mm, v(-26.47, 29.17) * mm, v(-26.47, 29.17) * mm, v(-26.47, 29.17) * mm, v(-26.64, 29.27) * mm, v(-26.85, 29.2) * mm, v(-26.95, 29.04) * mm, v(-26.95, 29.04) * mm, v(-26.96, 29.03) * mm, v(-27.55, 28) * mm, v(-27.56, 28) * mm, v(-27.56, 28) * mm, v(-27.65, 27.82) * mm, v(-27.6, 27.61) * mm, v(-27.43, 27.51) * mm, v(-27.43, 27.51) * mm, v(-27.42, 27.5) * mm, v(-26.95, 27.23) * mm, v(-26.9, 27.2) * mm, v(-26.9, 27.2) * mm, v(-26.9, 27.2) * mm]});
            skFitSpline(sketch, "E143", {"points": [v(-26.9, 27.2) * mm, v(-26.9, 27.2) * mm, v(-26.9, 27.2) * mm, v(-26.95, 27.22) * mm, v(-27.48, 27.4) * mm, v(-27.48, 27.4) * mm, v(-27.48, 27.4) * mm, v(-27.67, 27.45) * mm, v(-27.86, 27.35) * mm, v(-27.93, 27.17) * mm, v(-27.93, 27.17) * mm, v(-27.93, 27.16) * mm, v(-28.3, 26.03) * mm, v(-28.3, 26.02) * mm, v(-28.3, 26.01) * mm, v(-28.36, 25.83) * mm, v(-28.26, 25.63) * mm, v(-28.08, 25.57) * mm, v(-28.07, 25.57) * mm, v(-28.07, 25.57) * mm, v(-27.54, 25.4) * mm, v(-27.49, 25.38) * mm, v(-27.49, 25.38) * mm, v(-27.48, 25.38) * mm]});
            skFitSpline(sketch, "E144", {"points": [v(-27.48, 25.38) * mm, v(-27.49, 25.38) * mm, v(-27.49, 25.38) * mm, v(-27.55, 25.39) * mm, v(-28.1, 25.44) * mm, v(-28.1, 25.44) * mm, v(-28.1, 25.44) * mm, v(-28.3, 25.46) * mm, v(-28.47, 25.32) * mm, v(-28.49, 25.13) * mm, v(-28.49, 25.13) * mm, v(-28.49, 25.12) * mm, v(-28.61, 23.94) * mm, v(-28.61, 23.93) * mm, v(-28.62, 23.92) * mm, v(-28.63, 23.73) * mm, v(-28.5, 23.56) * mm, v(-28.3, 23.54) * mm]});
            skFitSpline(sketch, "E145", {"points": [v(-28.3, 23.54) * mm, v(-28.3, 23.54) * mm, v(-28.3, 23.54) * mm, v(-28.24, 23.53) * mm, v(-27.74, 23.48) * mm, v(-27.69, 23.48) * mm, v(-27.69, 23.48) * mm, v(-27.69, 23.48) * mm]});
            skFitSpline(sketch, "E146", {"points": [v(-27.69, 23.48) * mm, v(-27.69, 23.48) * mm, v(-27.69, 23.48) * mm, v(-27.75, 23.47) * mm, v(-28.3, 23.41) * mm, v(-28.3, 23.41) * mm, v(-28.3, 23.41) * mm, v(-28.5, 23.39) * mm, v(-28.63, 23.22) * mm, v(-28.61, 23.02) * mm, v(-28.61, 23.02) * mm, v(-28.61, 23.01) * mm, v(-28.49, 21.83) * mm, v(-28.49, 21.82) * mm, v(-28.49, 21.82) * mm, v(-28.47, 21.63) * mm, v(-28.3, 21.49) * mm, v(-28.1, 21.5) * mm, v(-28.1, 21.5) * mm, v(-28.1, 21.5) * mm, v(-27.55, 21.56) * mm, v(-27.49, 21.57) * mm, v(-27.49, 21.57) * mm, v(-27.48, 21.57) * mm]});
            skFitSpline(sketch, "E147", {"points": [v(-27.48, 21.57) * mm, v(-27.49, 21.57) * mm, v(-27.49, 21.57) * mm, v(-27.54, 21.55) * mm, v(-28.07, 21.38) * mm, v(-28.07, 21.38) * mm, v(-28.08, 21.38) * mm, v(-28.26, 21.32) * mm, v(-28.36, 21.12) * mm, v(-28.3, 20.94) * mm, v(-28.3, 20.94) * mm, v(-28.3, 20.92) * mm, v(-27.93, 19.8) * mm, v(-27.93, 19.78) * mm, v(-27.93, 19.78) * mm, v(-27.86, 19.6) * mm, v(-27.67, 19.5) * mm, v(-27.48, 19.56) * mm, v(-27.48, 19.56) * mm, v(-27.48, 19.56) * mm, v(-26.95, 19.73) * mm, v(-26.9, 19.75) * mm, v(-26.9, 19.75) * mm, v(-26.9, 19.75) * mm]});
            skFitSpline(sketch, "E148", {"points": [v(-26.9, 19.75) * mm, v(-26.9, 19.75) * mm, v(-26.9, 19.75) * mm, v(-26.95, 19.72) * mm, v(-27.42, 19.44) * mm, v(-27.43, 19.44) * mm, v(-27.43, 19.44) * mm, v(-27.6, 19.34) * mm, v(-27.65, 19.13) * mm, v(-27.56, 18.96) * mm, v(-27.56, 18.96) * mm, v(-27.55, 18.95) * mm, v(-26.96, 17.92) * mm, v(-26.95, 17.9) * mm, v(-26.95, 17.9) * mm, v(-26.85, 17.74) * mm, v(-26.64, 17.68) * mm, v(-26.47, 17.78) * mm, v(-26.47, 17.78) * mm, v(-26.47, 17.78) * mm, v(-25.99, 18.06) * mm, v(-25.94, 18.09) * mm, v(-25.94, 18.09) * mm, v(-25.94, 18.1) * mm]});
            skFitSpline(sketch, "E149", {"points": [v(-25.94, 18.1) * mm, v(-25.94, 18.09) * mm, v(-25.94, 18.09) * mm, v(-25.98, 18.05) * mm, v(-26.4, 17.68) * mm, v(-26.4, 17.68) * mm, v(-26.4, 17.67) * mm, v(-26.54, 17.54) * mm, v(-26.55, 17.32) * mm, v(-26.42, 17.18) * mm, v(-26.42, 17.18) * mm, v(-26.41, 17.17) * mm, v(-25.62, 16.29) * mm, v(-25.61, 16.28) * mm, v(-25.61, 16.28) * mm, v(-25.48, 16.13) * mm, v(-25.26, 16.12) * mm, v(-25.12, 16.25) * mm, v(-25.11, 16.25) * mm, v(-25.1, 16.26) * mm, v(-24.7, 16.63) * mm, v(-24.65, 16.67) * mm, v(-24.65, 16.67) * mm, v(-24.65, 16.67) * mm]});
            skFitSpline(sketch, "E150", {"points": [v(-24.65, 16.67) * mm, v(-24.65, 16.67) * mm, v(-24.65, 16.67) * mm, v(-24.7, 16.62) * mm, v(-25.01, 16.17) * mm, v(-25.02, 16.17) * mm, v(-25.02, 16.16) * mm, v(-25.13, 16) * mm, v(-25.1, 15.79) * mm, v(-24.94, 15.67) * mm, v(-24.94, 15.67) * mm, v(-24.93, 15.67) * mm, v(-23.97, 14.97) * mm, v(-23.96, 14.96) * mm, v(-23.96, 14.96) * mm, v(-23.8, 14.85) * mm, v(-23.58, 14.88) * mm, v(-23.47, 15.04) * mm, v(-23.47, 15.04) * mm, v(-23.46, 15.04) * mm, v(-23.14, 15.5) * mm, v(-23.1, 15.54) * mm, v(-23.1, 15.54) * mm, v(-23.1, 15.54) * mm]});
            skFitSpline(sketch, "E151", {"points": [v(-23.1, 15.54) * mm, v(-23.1, 15.54) * mm, v(-23.1, 15.54) * mm, v(-23.13, 15.48) * mm, v(-23.35, 14.98) * mm, v(-23.36, 14.98) * mm, v(-23.36, 14.97) * mm, v(-23.43, 14.8) * mm, v(-23.35, 14.6) * mm, v(-23.18, 14.51) * mm, v(-23.18, 14.51) * mm, v(-23.17, 14.5) * mm, v(-22.08, 14.02) * mm, v(-22.07, 14.02) * mm, v(-22.07, 14.02) * mm, v(-21.9, 13.94) * mm, v(-21.69, 14.02) * mm, v(-21.6, 14.2) * mm, v(-21.6, 14.2) * mm, v(-21.6, 14.2) * mm, v(-21.38, 14.7) * mm, v(-21.36, 14.76) * mm, v(-21.36, 14.76) * mm, v(-21.35, 14.76) * mm]});
            skFitSpline(sketch, "E152", {"points": [v(-21.35, 14.76) * mm, v(-21.35, 14.76) * mm, v(-21.35, 14.76) * mm, v(-21.37, 14.7) * mm, v(-21.48, 14.16) * mm, v(-21.48, 14.16) * mm, v(-21.48, 14.15) * mm, v(-21.52, 13.97) * mm, v(-21.4, 13.78) * mm, v(-21.21, 13.74) * mm, v(-21.21, 13.74) * mm, v(-21.2, 13.74) * mm, v(-20.04, 13.49) * mm, v(-20.03, 13.49) * mm, v(-20.03, 13.49) * mm, v(-19.84, 13.45) * mm, v(-19.65, 13.57) * mm, v(-19.61, 13.76) * mm, v(-19.6, 13.76) * mm, v(-19.6, 13.76) * mm, v(-19.5, 14.3) * mm, v(-19.48, 14.36) * mm, v(-19.48, 14.36) * mm, v(-19.48, 14.36) * mm]});
            skFitSpline(sketch, "E153", {"points": [v(-19.48, 14.36) * mm, v(-19.48, 14.36) * mm, v(-19.48, 14.36) * mm, v(-19.48, 14.3) * mm, v(-19.48, 13.75) * mm, v(-19.48, 13.74) * mm, v(-19.48, 13.74) * mm, v(-19.48, 13.55) * mm, v(-19.32, 13.4) * mm, v(-19.13, 13.4) * mm, v(-19.13, 13.4) * mm, v(-19.12, 13.4) * mm, v(-17.93, 13.4) * mm, v(-17.92, 13.4) * mm, v(-17.92, 13.4) * mm, v(-17.72, 13.4) * mm, v(-17.57, 13.55) * mm, v(-17.57, 13.74) * mm, v(-17.57, 13.74) * mm, v(-17.57, 13.75) * mm, v(-17.57, 14.3) * mm, v(-17.57, 14.36) * mm, v(-17.57, 14.36) * mm, v(-17.57, 14.36) * mm]});
            skFitSpline(sketch, "E154", {"points": [v(-17.57, 14.36) * mm, v(-17.57, 14.36) * mm, v(-17.57, 14.36) * mm, v(-17.55, 14.3) * mm, v(-17.44, 13.76) * mm, v(-17.44, 13.76) * mm, v(-17.44, 13.76) * mm, v(-17.4, 13.57) * mm, v(-17.2, 13.45) * mm, v(-17.02, 13.49) * mm, v(-17.02, 13.49) * mm, v(-17, 13.49) * mm, v(-15.85, 13.74) * mm, v(-15.83, 13.74) * mm, v(-15.83, 13.74) * mm, v(-15.64, 13.78) * mm, v(-15.52, 13.97) * mm, v(-15.56, 14.15) * mm, v(-15.56, 14.16) * mm, v(-15.56, 14.16) * mm, v(-15.68, 14.7) * mm, v(-15.7, 14.76) * mm, v(-15.7, 14.76) * mm, v(-15.7, 14.76) * mm]});
            skFitSpline(sketch, "E155", {"points": [v(-15.7, 14.76) * mm, v(-15.7, 14.76) * mm, v(-15.7, 14.76) * mm, v(-15.67, 14.7) * mm, v(-15.44, 14.2) * mm, v(-15.44, 14.2) * mm, v(-15.44, 14.2) * mm, v(-15.36, 14.02) * mm, v(-15.15, 13.94) * mm, v(-14.98, 14.02) * mm, v(-14.98, 14.02) * mm, v(-14.96, 14.02) * mm, v(-13.88, 14.5) * mm, v(-13.87, 14.51) * mm, v(-13.87, 14.51) * mm, v(-13.7, 14.6) * mm, v(-13.61, 14.8) * mm, v(-13.69, 14.97) * mm, v(-13.7, 14.98) * mm, v(-13.7, 14.98) * mm, v(-13.92, 15.48) * mm, v(-13.94, 15.54) * mm, v(-13.94, 15.54) * mm, v(-13.94, 15.54) * mm]});
            skFitSpline(sketch, "E156", {"points": [v(-13.94, 15.54) * mm, v(-13.94, 15.54) * mm, v(-13.94, 15.54) * mm, v(-13.9, 15.5) * mm, v(-13.58, 15.04) * mm, v(-13.58, 15.04) * mm, v(-13.58, 15.04) * mm, v(-13.46, 14.88) * mm, v(-13.24, 14.85) * mm, v(-13.09, 14.96) * mm, v(-13.09, 14.96) * mm, v(-13.08, 14.97) * mm, v(-12.12, 15.67) * mm, v(-12.1, 15.67) * mm, v(-12.1, 15.67) * mm, v(-11.95, 15.79) * mm, v(-11.92, 16) * mm, v(-12.03, 16.16) * mm, v(-12.03, 16.17) * mm, v(-12.03, 16.17) * mm, v(-12.36, 16.62) * mm, v(-12.4, 16.67) * mm, v(-12.4, 16.67) * mm, v(-12.4, 16.67) * mm]});
            skFitSpline(sketch, "E157", {"points": [v(-12.4, 16.67) * mm, v(-12.4, 16.67) * mm, v(-12.4, 16.67) * mm, v(-12.35, 16.63) * mm, v(-11.94, 16.26) * mm, v(-11.93, 16.25) * mm, v(-11.93, 16.25) * mm, v(-11.79, 16.12) * mm, v(-11.57, 16.13) * mm, v(-11.44, 16.28) * mm, v(-11.44, 16.28) * mm, v(-11.43, 16.29) * mm, v(-10.63, 17.17) * mm, v(-10.62, 17.18) * mm, v(-10.62, 17.18) * mm, v(-10.5, 17.32) * mm, v(-10.5, 17.54) * mm, v(-10.65, 17.67) * mm, v(-10.65, 17.68) * mm, v(-10.66, 17.68) * mm, v(-11.07, 18.05) * mm, v(-11.11, 18.09) * mm, v(-11.11, 18.09) * mm, v(-11.11, 18.1) * mm]});
            skFitSpline(sketch, "E158", {"points": [v(-11.11, 18.1) * mm, v(-11.11, 18.09) * mm, v(-11.11, 18.09) * mm, v(-11.06, 18.06) * mm, v(-10.58, 17.78) * mm, v(-10.57, 17.78) * mm, v(-10.57, 17.78) * mm, v(-10.4, 17.68) * mm, v(-10.2, 17.74) * mm, v(-10.1, 17.9) * mm, v(-10.1, 17.9) * mm, v(-10.09, 17.92) * mm, v(-9.5, 18.95) * mm, v(-9.49, 18.96) * mm, v(-9.49, 18.96) * mm, v(-9.4, 19.13) * mm, v(-9.45, 19.34) * mm, v(-9.62, 19.44) * mm, v(-9.62, 19.44) * mm, v(-9.62, 19.44) * mm, v(-10.1, 19.72) * mm, v(-10.15, 19.75) * mm, v(-10.15, 19.75) * mm, v(-10.15, 19.75) * mm]});
            skFitSpline(sketch, "E159", {"points": [v(-10.15, 19.75) * mm, v(-10.15, 19.75) * mm, v(-10.15, 19.75) * mm, v(-10.1, 19.73) * mm, v(-9.57, 19.56) * mm, v(-9.56, 19.56) * mm, v(-9.56, 19.56) * mm, v(-9.38, 19.5) * mm, v(-9.18, 19.6) * mm, v(-9.12, 19.78) * mm, v(-9.12, 19.78) * mm, v(-9.12, 19.8) * mm, v(-8.75, 20.92) * mm, v(-8.75, 20.94) * mm, v(-8.75, 20.94) * mm, v(-8.69, 21.12) * mm, v(-8.79, 21.32) * mm, v(-8.97, 21.38) * mm, v(-8.97, 21.38) * mm, v(-8.98, 21.38) * mm, v(-9.5, 21.55) * mm, v(-9.56, 21.57) * mm, v(-9.56, 21.57) * mm, v(-9.56, 21.57) * mm]});
            skFitSpline(sketch, "E160", {"points": [v(-9.56, 21.57) * mm, v(-9.56, 21.57) * mm, v(-9.56, 21.57) * mm, v(-9.5, 21.56) * mm, v(-8.95, 21.5) * mm, v(-8.95, 21.5) * mm, v(-8.94, 21.5) * mm, v(-8.75, 21.49) * mm, v(-8.58, 21.63) * mm, v(-8.56, 21.82) * mm, v(-8.56, 21.82) * mm, v(-8.56, 21.83) * mm, v(-8.43, 23.01) * mm, v(-8.43, 23.02) * mm, v(-8.43, 23.03) * mm, v(-8.42, 23.22) * mm, v(-8.56, 23.4) * mm, v(-8.75, 23.41) * mm]});
            skFitSpline(sketch, "E161", {"points": [v(16.68, 18.54) * mm, v(14.63, 18.54) * mm, v(12.75, 19.85) * mm, v(12.04, 21.78) * mm]});
            skFitSpline(sketch, "E162", {"points": [v(12.04, 21.78) * mm, v(11.33, 23.73) * mm, v(11.94, 25.97) * mm, v(13.54, 27.3) * mm]});
            skFitSpline(sketch, "E163", {"points": [v(13.54, 27.3) * mm, v(15.14, 28.61) * mm, v(17.47, 28.78) * mm, v(19.24, 27.7) * mm, v(21.01, 26.63) * mm, v(21.94, 24.51) * mm, v(21.52, 22.48) * mm]});
            skFitSpline(sketch, "E164", {"points": [v(21.52, 22.48) * mm, v(21.06, 20.21) * mm, v(19, 18.54) * mm, v(16.68, 18.54) * mm]});
            skFitSpline(sketch, "E165", {"points": [v(16.68, 27.16) * mm, v(15.16, 27.16) * mm, v(13.76, 26.19) * mm, v(13.22, 24.76) * mm]});
            skFitSpline(sketch, "E166", {"points": [v(13.22, 24.76) * mm, v(12.68, 23.3) * mm, v(13.14, 21.61) * mm, v(14.33, 20.62) * mm]});
            skFitSpline(sketch, "E167", {"points": [v(14.33, 20.62) * mm, v(15.52, 19.64) * mm, v(17.25, 19.51) * mm, v(18.58, 20.3) * mm]});
            skFitSpline(sketch, "E168", {"points": [v(18.58, 20.3) * mm, v(19.9, 21.1) * mm, v(20.6, 22.67) * mm, v(20.3, 24.18) * mm]});
            skFitSpline(sketch, "E169", {"points": [v(20.3, 24.18) * mm, v(19.98, 25.89) * mm, v(18.43, 27.16) * mm, v(16.68, 27.16) * mm]});
            skFitSpline(sketch, "E170", {"points": [v(26.46, 23.41) * mm, v(26.46, 23.41) * mm, v(26.46, 23.41) * mm, v(26.4, 23.42) * mm, v(25.9, 23.47) * mm, v(25.85, 23.48) * mm, v(25.85, 23.48) * mm, v(25.85, 23.48) * mm]});
            skFitSpline(sketch, "E171", {"points": [v(25.85, 23.48) * mm, v(25.85, 23.48) * mm, v(25.85, 23.48) * mm, v(25.9, 23.48) * mm, v(26.46, 23.54) * mm, v(26.46, 23.54) * mm, v(26.46, 23.54) * mm, v(26.66, 23.56) * mm, v(26.8, 23.73) * mm, v(26.78, 23.93) * mm, v(26.78, 23.93) * mm, v(26.77, 23.94) * mm, v(26.65, 25.12) * mm, v(26.65, 25.13) * mm, v(26.65, 25.13) * mm, v(26.63, 25.32) * mm, v(26.46, 25.46) * mm, v(26.26, 25.44) * mm, v(26.26, 25.44) * mm, v(26.26, 25.44) * mm, v(25.7, 25.39) * mm, v(25.65, 25.38) * mm, v(25.65, 25.38) * mm, v(25.65, 25.38) * mm]});
            skFitSpline(sketch, "E172", {"points": [v(25.65, 25.38) * mm, v(25.65, 25.38) * mm, v(25.65, 25.38) * mm, v(25.7, 25.4) * mm, v(26.23, 25.57) * mm, v(26.23, 25.57) * mm, v(26.24, 25.57) * mm, v(26.42, 25.63) * mm, v(26.52, 25.83) * mm, v(26.46, 26.01) * mm, v(26.46, 26.02) * mm, v(26.46, 26.03) * mm, v(26.1, 27.16) * mm, v(26.09, 27.17) * mm, v(26.09, 27.17) * mm, v(26.02, 27.35) * mm, v(25.83, 27.45) * mm, v(25.64, 27.4) * mm, v(25.64, 27.4) * mm, v(25.64, 27.4) * mm, v(25.11, 27.22) * mm, v(25.06, 27.2) * mm, v(25.06, 27.2) * mm, v(25.05, 27.2) * mm]});
            skFitSpline(sketch, "E173", {"points": [v(25.05, 27.2) * mm, v(25.06, 27.2) * mm, v(25.06, 27.2) * mm, v(25.1, 27.23) * mm, v(25.58, 27.5) * mm, v(25.6, 27.51) * mm, v(25.6, 27.51) * mm, v(25.76, 27.61) * mm, v(25.82, 27.82) * mm, v(25.72, 28) * mm, v(25.72, 28) * mm, v(25.71, 28) * mm, v(25.12, 29.03) * mm, v(25.11, 29.04) * mm, v(25.11, 29.04) * mm, v(25.01, 29.2) * mm, v(24.8, 29.27) * mm, v(24.63, 29.17) * mm, v(24.63, 29.17) * mm, v(24.63, 29.17) * mm, v(24.15, 28.9) * mm, v(24.1, 28.86) * mm, v(24.1, 28.86) * mm, v(24.1, 28.86) * mm]});
            skFitSpline(sketch, "E174", {"points": [v(24.1, 28.86) * mm, v(24.1, 28.86) * mm, v(24.1, 28.86) * mm, v(24.14, 28.9) * mm, v(24.55, 29.27) * mm, v(24.56, 29.27) * mm, v(24.56, 29.28) * mm, v(24.7, 29.4) * mm, v(24.71, 29.63) * mm, v(24.58, 29.77) * mm, v(24.58, 29.77) * mm, v(24.57, 29.78) * mm, v(23.78, 30.66) * mm, v(23.77, 30.67) * mm, v(23.77, 30.67) * mm, v(23.64, 30.82) * mm, v(23.42, 30.83) * mm, v(23.28, 30.7) * mm, v(23.27, 30.7) * mm, v(23.27, 30.7) * mm, v(22.86, 30.33) * mm, v(22.82, 30.28) * mm, v(22.82, 30.28) * mm, v(22.81, 30.28) * mm]});
            skFitSpline(sketch, "E175", {"points": [v(22.81, 30.28) * mm, v(22.82, 30.28) * mm, v(22.82, 30.28) * mm, v(22.85, 30.33) * mm, v(23.18, 30.78) * mm, v(23.18, 30.78) * mm, v(23.18, 30.79) * mm, v(23.3, 30.94) * mm, v(23.26, 31.16) * mm, v(23.1, 31.28) * mm, v(23.1, 31.28) * mm, v(23.1, 31.28) * mm, v(22.13, 31.98) * mm, v(22.12, 31.99) * mm, v(22.12, 31.99) * mm, v(21.96, 32.1) * mm, v(21.74, 32.07) * mm, v(21.63, 31.91) * mm, v(21.63, 31.91) * mm, v(21.63, 31.9) * mm, v(21.3, 31.46) * mm, v(21.27, 31.41) * mm, v(21.27, 31.41) * mm, v(21.26, 31.4) * mm]});
            skFitSpline(sketch, "E176", {"points": [v(21.26, 31.4) * mm, v(21.27, 31.41) * mm, v(21.27, 31.41) * mm, v(21.3, 31.47) * mm, v(21.51, 31.97) * mm, v(21.52, 31.98) * mm, v(21.52, 31.98) * mm, v(21.6, 32.15) * mm, v(21.52, 32.36) * mm, v(21.34, 32.44) * mm, v(21.34, 32.44) * mm, v(21.33, 32.45) * mm, v(20.24, 32.93) * mm, v(20.23, 32.93) * mm, v(20.23, 32.93) * mm, v(20.05, 33.01) * mm, v(19.85, 32.93) * mm, v(19.77, 32.76) * mm, v(19.77, 32.75) * mm, v(19.76, 32.75) * mm, v(19.54, 32.25) * mm, v(19.52, 32.2) * mm, v(19.52, 32.19) * mm, v(19.52, 32.19) * mm]});
            skFitSpline(sketch, "E177", {"points": [v(19.52, 32.19) * mm, v(19.52, 32.2) * mm, v(19.52, 32.2) * mm, v(19.53, 32.25) * mm, v(19.64, 32.79) * mm, v(19.64, 32.8) * mm, v(19.64, 32.8) * mm, v(19.68, 32.99) * mm, v(19.56, 33.17) * mm, v(19.37, 33.21) * mm, v(19.37, 33.21) * mm, v(19.36, 33.21) * mm, v(18.2, 33.46) * mm, v(18.19, 33.46) * mm, v(18.19, 33.46) * mm, v(18, 33.5) * mm, v(17.81, 33.38) * mm, v(17.77, 33.2) * mm, v(17.77, 33.2) * mm, v(17.77, 33.19) * mm, v(17.65, 32.65) * mm, v(17.64, 32.59) * mm, v(17.64, 32.59) * mm, v(17.64, 32.59) * mm]});
            skFitSpline(sketch, "E178", {"points": [v(17.64, 32.59) * mm, v(17.64, 32.59) * mm, v(17.64, 32.59) * mm, v(17.64, 32.65) * mm, v(17.64, 33.2) * mm, v(17.64, 33.2) * mm, v(17.64, 33.2) * mm, v(17.64, 33.4) * mm, v(17.48, 33.56) * mm, v(17.3, 33.56) * mm, v(17.29, 33.56) * mm, v(17.28, 33.56) * mm, v(16.1, 33.56) * mm, v(16.08, 33.56) * mm, v(16.08, 33.56) * mm, v(15.88, 33.56) * mm, v(15.73, 33.4) * mm, v(15.73, 33.2) * mm, v(15.73, 33.2) * mm, v(15.73, 33.2) * mm, v(15.73, 32.65) * mm, v(15.73, 32.59) * mm, v(15.73, 32.59) * mm, v(15.73, 32.59) * mm]});
            skFitSpline(sketch, "E179", {"points": [v(15.73, 32.59) * mm, v(15.73, 32.59) * mm, v(15.73, 32.59) * mm, v(15.71, 32.65) * mm, v(15.6, 33.19) * mm, v(15.6, 33.2) * mm, v(15.6, 33.2) * mm, v(15.56, 33.38) * mm, v(15.37, 33.5) * mm, v(15.18, 33.46) * mm, v(15.18, 33.46) * mm, v(15.17, 33.46) * mm, v(14, 33.21) * mm, v(14, 33.21) * mm, v(14, 33.21) * mm, v(13.8, 33.17) * mm, v(13.69, 32.99) * mm, v(13.72, 32.8) * mm, v(13.72, 32.8) * mm, v(13.73, 32.79) * mm, v(13.84, 32.25) * mm, v(13.85, 32.2) * mm, v(13.85, 32.19) * mm, v(13.85, 32.19) * mm]});
            skFitSpline(sketch, "E180", {"points": [v(13.85, 32.19) * mm, v(13.85, 32.19) * mm, v(13.85, 32.19) * mm, v(13.83, 32.25) * mm, v(13.6, 32.75) * mm, v(13.6, 32.75) * mm, v(13.6, 32.76) * mm, v(13.52, 32.93) * mm, v(13.31, 33.01) * mm, v(13.14, 32.93) * mm, v(13.14, 32.93) * mm, v(13.12, 32.93) * mm, v(12.04, 32.45) * mm, v(12.03, 32.44) * mm, v(12.03, 32.44) * mm, v(11.85, 32.36) * mm, v(11.77, 32.15) * mm, v(11.85, 31.98) * mm, v(11.85, 31.98) * mm, v(11.85, 31.97) * mm, v(12.08, 31.47) * mm, v(12.1, 31.41) * mm, v(12.1, 31.41) * mm, v(12.1, 31.4) * mm]});
            skFitSpline(sketch, "E181", {"points": [v(12.1, 31.4) * mm, v(12.1, 31.41) * mm, v(12.1, 31.41) * mm, v(12.07, 31.46) * mm, v(11.74, 31.9) * mm, v(11.74, 31.91) * mm, v(11.74, 31.91) * mm, v(11.62, 32.07) * mm, v(11.4, 32.1) * mm, v(11.25, 31.99) * mm, v(11.25, 31.99) * mm, v(11.24, 31.98) * mm, v(10.28, 31.28) * mm, v(10.27, 31.28) * mm, v(10.27, 31.28) * mm, v(10.11, 31.16) * mm, v(10.08, 30.94) * mm, v(10.19, 30.79) * mm, v(10.19, 30.78) * mm, v(10.2, 30.78) * mm, v(10.52, 30.33) * mm, v(10.55, 30.28) * mm, v(10.55, 30.28) * mm, v(10.55, 30.28) * mm]});
            skFitSpline(sketch, "E182", {"points": [v(10.55, 30.28) * mm, v(10.55, 30.28) * mm, v(10.55, 30.28) * mm, v(10.5, 30.33) * mm, v(10.1, 30.7) * mm, v(10.1, 30.7) * mm, v(10.1, 30.7) * mm, v(9.95, 30.83) * mm, v(9.73, 30.82) * mm, v(9.6, 30.67) * mm, v(9.6, 30.67) * mm, v(9.59, 30.66) * mm, v(8.8, 29.78) * mm, v(8.79, 29.77) * mm, v(8.78, 29.77) * mm, v(8.66, 29.63) * mm, v(8.67, 29.4) * mm, v(8.81, 29.28) * mm, v(8.81, 29.27) * mm, v(8.82, 29.27) * mm, v(9.23, 28.9) * mm, v(9.27, 28.86) * mm, v(9.27, 28.86) * mm, v(9.27, 28.86) * mm]});
            skFitSpline(sketch, "E183", {"points": [v(9.27, 28.86) * mm, v(9.27, 28.86) * mm, v(9.27, 28.86) * mm, v(9.22, 28.9) * mm, v(8.74, 29.17) * mm, v(8.74, 29.17) * mm, v(8.73, 29.17) * mm, v(8.57, 29.27) * mm, v(8.35, 29.2) * mm, v(8.26, 29.04) * mm, v(8.25, 29.04) * mm, v(8.25, 29.03) * mm, v(7.66, 28) * mm, v(7.65, 28) * mm, v(7.65, 28) * mm, v(7.55, 27.82) * mm, v(7.61, 27.61) * mm, v(7.78, 27.51) * mm, v(7.78, 27.51) * mm, v(7.78, 27.5) * mm, v(8.26, 27.23) * mm, v(8.31, 27.2) * mm, v(8.31, 27.2) * mm, v(8.31, 27.2) * mm]});
            skFitSpline(sketch, "E184", {"points": [v(8.31, 27.2) * mm, v(8.31, 27.2) * mm, v(8.31, 27.2) * mm, v(8.26, 27.22) * mm, v(7.73, 27.4) * mm, v(7.73, 27.4) * mm, v(7.72, 27.4) * mm, v(7.54, 27.45) * mm, v(7.34, 27.35) * mm, v(7.28, 27.17) * mm, v(7.28, 27.17) * mm, v(7.28, 27.16) * mm, v(6.91, 26.03) * mm, v(6.9, 26.02) * mm, v(6.9, 26.01) * mm, v(6.85, 25.83) * mm, v(6.95, 25.63) * mm, v(7.13, 25.57) * mm, v(7.13, 25.57) * mm, v(7.14, 25.57) * mm, v(7.66, 25.4) * mm, v(7.72, 25.38) * mm, v(7.72, 25.38) * mm, v(7.72, 25.38) * mm]});
            skFitSpline(sketch, "E185", {"points": [v(7.72, 25.38) * mm, v(7.72, 25.38) * mm, v(7.72, 25.38) * mm, v(7.66, 25.39) * mm, v(7.11, 25.44) * mm, v(7.1, 25.44) * mm, v(7.1, 25.44) * mm, v(6.91, 25.46) * mm, v(6.74, 25.32) * mm, v(6.72, 25.13) * mm, v(6.72, 25.13) * mm, v(6.72, 25.12) * mm, v(6.6, 23.94) * mm, v(6.6, 23.93) * mm, v(6.6, 23.92) * mm, v(6.58, 23.73) * mm, v(6.72, 23.56) * mm, v(6.9, 23.54) * mm]});
            skFitSpline(sketch, "E186", {"points": [v(6.9, 23.54) * mm, v(6.9, 23.54) * mm, v(6.9, 23.54) * mm, v(6.97, 23.53) * mm, v(7.46, 23.48) * mm, v(7.52, 23.48) * mm, v(7.52, 23.48) * mm, v(7.52, 23.48) * mm]});
            skFitSpline(sketch, "E187", {"points": [v(7.52, 23.48) * mm, v(7.52, 23.48) * mm, v(7.52, 23.48) * mm, v(7.46, 23.47) * mm, v(6.91, 23.41) * mm, v(6.9, 23.41) * mm, v(6.9, 23.41) * mm, v(6.71, 23.39) * mm, v(6.57, 23.22) * mm, v(6.6, 23.02) * mm, v(6.6, 23.02) * mm, v(6.6, 23.01) * mm, v(6.72, 21.83) * mm, v(6.72, 21.82) * mm, v(6.72, 21.82) * mm, v(6.74, 21.63) * mm, v(6.91, 21.49) * mm, v(7.1, 21.5) * mm, v(7.1, 21.5) * mm, v(7.11, 21.5) * mm, v(7.66, 21.56) * mm, v(7.72, 21.57) * mm, v(7.72, 21.57) * mm, v(7.72, 21.57) * mm]});
            skFitSpline(sketch, "E188", {"points": [v(7.72, 21.57) * mm, v(7.72, 21.57) * mm, v(7.72, 21.57) * mm, v(7.66, 21.55) * mm, v(7.14, 21.38) * mm, v(7.13, 21.38) * mm, v(7.13, 21.38) * mm, v(6.95, 21.32) * mm, v(6.85, 21.12) * mm, v(6.9, 20.94) * mm, v(6.9, 20.94) * mm, v(6.91, 20.92) * mm, v(7.28, 19.8) * mm, v(7.28, 19.78) * mm, v(7.28, 19.78) * mm, v(7.34, 19.6) * mm, v(7.54, 19.5) * mm, v(7.72, 19.56) * mm, v(7.73, 19.56) * mm, v(7.73, 19.56) * mm, v(8.26, 19.73) * mm, v(8.31, 19.75) * mm, v(8.31, 19.75) * mm, v(8.31, 19.75) * mm]});
            skFitSpline(sketch, "E189", {"points": [v(8.31, 19.75) * mm, v(8.31, 19.75) * mm, v(8.31, 19.75) * mm, v(8.26, 19.72) * mm, v(7.78, 19.44) * mm, v(7.78, 19.44) * mm, v(7.78, 19.44) * mm, v(7.61, 19.34) * mm, v(7.55, 19.13) * mm, v(7.65, 18.96) * mm, v(7.65, 18.96) * mm, v(7.66, 18.95) * mm, v(8.25, 17.92) * mm, v(8.25, 17.9) * mm, v(8.26, 17.9) * mm, v(8.35, 17.74) * mm, v(8.57, 17.68) * mm, v(8.73, 17.78) * mm, v(8.74, 17.78) * mm, v(8.74, 17.78) * mm, v(9.22, 18.06) * mm, v(9.27, 18.09) * mm, v(9.27, 18.09) * mm, v(9.27, 18.1) * mm]});
            skFitSpline(sketch, "E190", {"points": [v(9.27, 18.1) * mm, v(9.27, 18.09) * mm, v(9.27, 18.09) * mm, v(9.23, 18.05) * mm, v(8.82, 17.68) * mm, v(8.81, 17.68) * mm, v(8.81, 17.67) * mm, v(8.67, 17.54) * mm, v(8.66, 17.32) * mm, v(8.78, 17.18) * mm, v(8.79, 17.18) * mm, v(8.8, 17.17) * mm, v(9.59, 16.29) * mm, v(9.6, 16.28) * mm, v(9.6, 16.28) * mm, v(9.73, 16.13) * mm, v(9.95, 16.12) * mm, v(10.1, 16.25) * mm, v(10.1, 16.25) * mm, v(10.1, 16.26) * mm, v(10.5, 16.63) * mm, v(10.55, 16.67) * mm, v(10.55, 16.67) * mm, v(10.55, 16.67) * mm]});
            skFitSpline(sketch, "E191", {"points": [v(10.55, 16.67) * mm, v(10.55, 16.67) * mm, v(10.55, 16.67) * mm, v(10.52, 16.62) * mm, v(10.2, 16.17) * mm, v(10.19, 16.17) * mm, v(10.19, 16.16) * mm, v(10.08, 16) * mm, v(10.11, 15.79) * mm, v(10.27, 15.67) * mm, v(10.27, 15.67) * mm, v(10.28, 15.67) * mm, v(11.24, 14.97) * mm, v(11.25, 14.96) * mm, v(11.25, 14.96) * mm, v(11.4, 14.85) * mm, v(11.62, 14.88) * mm, v(11.74, 15.04) * mm, v(11.74, 15.04) * mm, v(11.74, 15.04) * mm, v(12.07, 15.5) * mm, v(12.1, 15.54) * mm, v(12.1, 15.54) * mm, v(12.1, 15.54) * mm]});
            skFitSpline(sketch, "E192", {"points": [v(12.1, 15.54) * mm, v(12.1, 15.54) * mm, v(12.1, 15.54) * mm, v(12.08, 15.48) * mm, v(11.85, 14.98) * mm, v(11.85, 14.98) * mm, v(11.85, 14.97) * mm, v(11.77, 14.8) * mm, v(11.85, 14.6) * mm, v(12.03, 14.51) * mm, v(12.03, 14.51) * mm, v(12.04, 14.5) * mm, v(13.12, 14.02) * mm, v(13.14, 14.02) * mm, v(13.14, 14.02) * mm, v(13.31, 13.94) * mm, v(13.52, 14.02) * mm, v(13.6, 14.2) * mm, v(13.6, 14.2) * mm, v(13.6, 14.2) * mm, v(13.83, 14.7) * mm, v(13.85, 14.76) * mm, v(13.85, 14.76) * mm, v(13.85, 14.76) * mm]});
            skFitSpline(sketch, "E193", {"points": [v(13.85, 14.76) * mm, v(13.85, 14.76) * mm, v(13.85, 14.76) * mm, v(13.84, 14.7) * mm, v(13.73, 14.16) * mm, v(13.72, 14.16) * mm, v(13.72, 14.15) * mm, v(13.69, 13.97) * mm, v(13.8, 13.78) * mm, v(14, 13.74) * mm, v(14, 13.74) * mm, v(14, 13.74) * mm, v(15.17, 13.49) * mm, v(15.18, 13.49) * mm, v(15.18, 13.49) * mm, v(15.37, 13.45) * mm, v(15.56, 13.57) * mm, v(15.6, 13.76) * mm, v(15.6, 13.76) * mm, v(15.6, 13.76) * mm, v(15.71, 14.3) * mm, v(15.73, 14.36) * mm, v(15.73, 14.36) * mm, v(15.73, 14.36) * mm]});
            skFitSpline(sketch, "E194", {"points": [v(15.73, 14.36) * mm, v(15.73, 14.36) * mm, v(15.73, 14.36) * mm, v(15.73, 14.3) * mm, v(15.73, 13.75) * mm, v(15.73, 13.74) * mm, v(15.73, 13.74) * mm, v(15.73, 13.55) * mm, v(15.88, 13.4) * mm, v(16.08, 13.4) * mm, v(16.08, 13.4) * mm, v(16.1, 13.4) * mm, v(17.28, 13.4) * mm, v(17.29, 13.4) * mm, v(17.3, 13.4) * mm, v(17.48, 13.4) * mm, v(17.64, 13.55) * mm, v(17.64, 13.74) * mm, v(17.64, 13.74) * mm, v(17.64, 13.75) * mm, v(17.64, 14.3) * mm, v(17.64, 14.36) * mm, v(17.64, 14.36) * mm, v(17.64, 14.36) * mm]});
            skFitSpline(sketch, "E195", {"points": [v(17.64, 14.36) * mm, v(17.64, 14.36) * mm, v(17.64, 14.36) * mm, v(17.65, 14.3) * mm, v(17.77, 13.76) * mm, v(17.77, 13.76) * mm, v(17.77, 13.76) * mm, v(17.81, 13.57) * mm, v(18, 13.45) * mm, v(18.19, 13.49) * mm, v(18.19, 13.49) * mm, v(18.2, 13.49) * mm, v(19.36, 13.74) * mm, v(19.37, 13.74) * mm, v(19.37, 13.74) * mm, v(19.56, 13.78) * mm, v(19.68, 13.97) * mm, v(19.64, 14.15) * mm, v(19.64, 14.16) * mm, v(19.64, 14.16) * mm, v(19.53, 14.7) * mm, v(19.52, 14.76) * mm, v(19.52, 14.76) * mm, v(19.52, 14.76) * mm]});
            skFitSpline(sketch, "E196", {"points": [v(19.52, 14.76) * mm, v(19.52, 14.76) * mm, v(19.52, 14.76) * mm, v(19.54, 14.7) * mm, v(19.76, 14.2) * mm, v(19.77, 14.2) * mm, v(19.77, 14.2) * mm, v(19.85, 14.02) * mm, v(20.05, 13.94) * mm, v(20.23, 14.02) * mm, v(20.23, 14.02) * mm, v(20.24, 14.02) * mm, v(21.33, 14.5) * mm, v(21.34, 14.51) * mm, v(21.34, 14.51) * mm, v(21.52, 14.6) * mm, v(21.6, 14.8) * mm, v(21.52, 14.97) * mm, v(21.52, 14.98) * mm, v(21.51, 14.98) * mm, v(21.3, 15.48) * mm, v(21.27, 15.54) * mm, v(21.27, 15.54) * mm, v(21.26, 15.54) * mm]});
            skFitSpline(sketch, "E197", {"points": [v(21.26, 15.54) * mm, v(21.27, 15.54) * mm, v(21.27, 15.54) * mm, v(21.3, 15.5) * mm, v(21.63, 15.04) * mm, v(21.63, 15.04) * mm, v(21.63, 15.04) * mm, v(21.74, 14.88) * mm, v(21.96, 14.85) * mm, v(22.12, 14.96) * mm, v(22.12, 14.96) * mm, v(22.13, 14.97) * mm, v(23.1, 15.67) * mm, v(23.1, 15.67) * mm, v(23.1, 15.67) * mm, v(23.26, 15.79) * mm, v(23.3, 16) * mm, v(23.18, 16.16) * mm, v(23.18, 16.17) * mm, v(23.18, 16.17) * mm, v(22.85, 16.62) * mm, v(22.82, 16.67) * mm, v(22.82, 16.67) * mm, v(22.81, 16.67) * mm]});
            skFitSpline(sketch, "E198", {"points": [v(22.81, 16.67) * mm, v(22.82, 16.67) * mm, v(22.82, 16.67) * mm, v(22.86, 16.63) * mm, v(23.27, 16.26) * mm, v(23.27, 16.25) * mm, v(23.28, 16.25) * mm, v(23.42, 16.12) * mm, v(23.64, 16.13) * mm, v(23.77, 16.28) * mm, v(23.77, 16.28) * mm, v(23.78, 16.29) * mm, v(24.57, 17.17) * mm, v(24.58, 17.18) * mm, v(24.58, 17.18) * mm, v(24.71, 17.32) * mm, v(24.7, 17.54) * mm, v(24.56, 17.67) * mm, v(24.56, 17.68) * mm, v(24.55, 17.68) * mm, v(24.14, 18.05) * mm, v(24.1, 18.09) * mm, v(24.1, 18.09) * mm, v(24.1, 18.1) * mm]});
            skFitSpline(sketch, "E199", {"points": [v(24.1, 18.1) * mm, v(24.1, 18.09) * mm, v(24.1, 18.09) * mm, v(24.15, 18.06) * mm, v(24.63, 17.78) * mm, v(24.63, 17.78) * mm, v(24.63, 17.78) * mm, v(24.8, 17.68) * mm, v(25.01, 17.74) * mm, v(25.11, 17.9) * mm, v(25.11, 17.9) * mm, v(25.12, 17.92) * mm, v(25.71, 18.95) * mm, v(25.72, 18.96) * mm, v(25.72, 18.96) * mm, v(25.82, 19.13) * mm, v(25.76, 19.34) * mm, v(25.6, 19.44) * mm, v(25.6, 19.44) * mm, v(25.58, 19.44) * mm, v(25.1, 19.72) * mm, v(25.06, 19.75) * mm, v(25.06, 19.75) * mm, v(25.05, 19.75) * mm]});
            skFitSpline(sketch, "E200", {"points": [v(25.05, 19.75) * mm, v(25.06, 19.75) * mm, v(25.06, 19.75) * mm, v(25.11, 19.73) * mm, v(25.64, 19.56) * mm, v(25.64, 19.56) * mm, v(25.64, 19.56) * mm, v(25.83, 19.5) * mm, v(26.02, 19.6) * mm, v(26.09, 19.78) * mm, v(26.09, 19.78) * mm, v(26.1, 19.8) * mm, v(26.46, 20.92) * mm, v(26.46, 20.94) * mm, v(26.46, 20.94) * mm, v(26.52, 21.12) * mm, v(26.42, 21.32) * mm, v(26.24, 21.38) * mm, v(26.23, 21.38) * mm, v(26.23, 21.38) * mm, v(25.7, 21.55) * mm, v(25.65, 21.57) * mm, v(25.65, 21.57) * mm, v(25.65, 21.57) * mm]});
            skFitSpline(sketch, "E201", {"points": [v(25.65, 21.57) * mm, v(25.65, 21.57) * mm, v(25.65, 21.57) * mm, v(25.7, 21.56) * mm, v(26.26, 21.5) * mm, v(26.26, 21.5) * mm, v(26.26, 21.5) * mm, v(26.46, 21.49) * mm, v(26.63, 21.63) * mm, v(26.65, 21.82) * mm, v(26.65, 21.82) * mm, v(26.65, 21.83) * mm, v(26.77, 23.01) * mm, v(26.78, 23.02) * mm, v(26.78, 23.03) * mm, v(26.8, 23.22) * mm, v(26.65, 23.4) * mm, v(26.46, 23.41) * mm]});
            skSolve(sketch);
        }
        {
            var Q0;
            Q0=makeQuery(id+"F4.imprint","IMPRINT",FACE,{"disambiguationData":[TD([[makeQuery(id+"F4.imprint","IMPRINT",EDGE,{"derivedFrom":sQuery(id+"F4.wireOp",EDGE,"E47")}),1.0]])]});
            var Q1;
            Q1=makeQuery(id+"F4.imprint","IMPRINT",FACE,{"disambiguationData":[TD([[makeQuery(id+"F4.imprint","IMPRINT",EDGE,{"derivedFrom":sQuery(id+"F4.wireOp",EDGE,"E119")}),1.0]])]});
            var Q2;
            Q2=makeQuery(id+"F4.imprint","IMPRINT",FACE,{"disambiguationData":[TD([[makeQuery(id+"F4.imprint","IMPRINT",EDGE,{"derivedFrom":sQuery(id+"F4.wireOp",EDGE,"E124")}),1.0]])]});
            var Q3;
            Q3=makeQuery(id+"F4.imprint","IMPRINT",FACE,{"disambiguationData":[TD([[makeQuery(id+"F4.imprint","IMPRINT",EDGE,{"derivedFrom":sQuery(id+"F4.wireOp",EDGE,"E18")}),1.0]])]});
            var Q4;
            Q4=makeQuery(id+"F4.imprint","IMPRINT",FACE,{"disambiguationData":[TD([[makeQuery(id+"F4.imprint","IMPRINT",EDGE,{"derivedFrom":sQuery(id+"F4.wireOp",EDGE,"E13")}),1.0]])]});
            var Q5;
            Q5=makeQuery(id+"F4.imprint","IMPRINT",FACE,{"disambiguationData":[TD([[makeQuery(id+"F4.imprint","IMPRINT",EDGE,{"derivedFrom":sQuery(id+"F4.wireOp",EDGE,"E5")}),1.0]])]});
            var Q6;
            Q6=makeQuery(id+"F4.imprint","IMPRINT",FACE,{"disambiguationData":[TD([[makeQuery(id+"F4.imprint","IMPRINT",EDGE,{"derivedFrom":sQuery(id+"F4.wireOp",EDGE,"E161")}),1.0]])]});
            var Q7;
            Q7=makeQuery(id+"F4.imprint","IMPRINT",FACE,{"disambiguationData":[TD([[makeQuery(id+"F4.imprint","IMPRINT",EDGE,{"derivedFrom":sQuery(id+"F4.wireOp",EDGE,"E165")}),1.0]])]});
            var Q8;
            Q8=makeQuery(id+"F4.imprint","IMPRINT",FACE,{"disambiguationData":[TD([[makeQuery(id+"F4.imprint","IMPRINT",EDGE,{"derivedFrom":sQuery(id+"F4.wireOp",EDGE,"E38")}),1.0]])]});
            var Q9;
            Q9=makeQuery(id+"F4.imprint","IMPRINT",FACE,{"disambiguationData":[TD([[makeQuery(id+"F4.imprint","IMPRINT",EDGE,{"derivedFrom":sQuery(id+"F4.wireOp",EDGE,"E35")}),1.0]])]});
            var Q10;
            Q10=makeQuery(id+"F4.imprint","IMPRINT",FACE,{"disambiguationData":[TD([[makeQuery(id+"F4.imprint","IMPRINT",EDGE,{"derivedFrom":sQuery(id+"F4.wireOp",EDGE,"E27")}),1.0]])]});
            extrude(context, id + "F5", {"entities" : qUnion([Q0, Q1, Q2, Q3, Q4, Q5, Q6, Q7, Q8, Q9, Q10]), "operationType" : NewBodyOperationType.REMOVE, "oppositeDirection" : true, "depth" : 3.8 * mm, "offsetDistance" : 25.4 * mm});
        }
        {
            var Q0;
            Q0=makeQuery(id+"F3.opExtrude","SWEPT_EDGE",EDGE,{"disambiguationData":[OSD([sQuery(id+"F2.wireOp",EDGE,"E4.top"),sQuery(id+"F2.wireOp",EDGE,"E4.left")])]});
            var Q1;
            Q1=makeQuery(id+"F3.opExtrude","SWEPT_EDGE",EDGE,{"disambiguationData":[OSD([sQuery(id+"F2.wireOp",EDGE,"E4.top"),sQuery(id+"F2.wireOp",EDGE,"E4.right")])]});
            fillet(context, id + "F6", {"entities" : qUnion([Q0, Q1]), "radius" : 5.08 * mm, "tangentPropagation" : true, "allowEdgeOverflow" : false});
        }
        {
            var Q0;
            Q0=makeQuery(id+"F3.opExtrude","CAP_FACE",FACE,{"disambiguationData":[OSD([sQuery(id+"F2.wireOp",EDGE,"E4.bottom"),sQuery(id+"F2.wireOp",EDGE,"E4.top"),sQuery(id+"F2.wireOp",EDGE,"E4.left"),sQuery(id+"F2.wireOp",EDGE,"E4.right")])],"isStart":false});
            var sketch = newSketch(context, id + "F7", { "sketchPlane" : qUnion([Q0])});
            skCircle(sketch, "E202", {"center": v(-33.15, 64.77) * mm, "radius": 2.25 * mm});
            skCircle(sketch, "E203", {"center": v(33.15, 64.77) * mm, "radius": 2.25 * mm});
            skSolve(sketch);
        }
        {
            var Q0;
            Q0=makeQuery(id+"F7.imprint","IMPRINT",FACE,{"disambiguationData":[TD([[makeQuery(id+"F7.imprint","IMPRINT",EDGE,{"derivedFrom":sQuery(id+"F7.wireOp",EDGE,"E202")}),1.0]])]});
            var Q1;
            Q1=makeQuery(id+"F7.imprint","IMPRINT",FACE,{"disambiguationData":[TD([[makeQuery(id+"F7.imprint","IMPRINT",EDGE,{"derivedFrom":sQuery(id+"F7.wireOp",EDGE,"E203")}),1.0]])]});
            extrude(context, id + "F8", {"entities" : qUnion([Q0, Q1]), "operationType" : NewBodyOperationType.REMOVE, "endBound" : BoundingType.UP_TO_NEXT, "oppositeDirection" : true, "depth" : 25.4 * mm, "offsetDistance" : 25.4 * mm});
        }
    });
